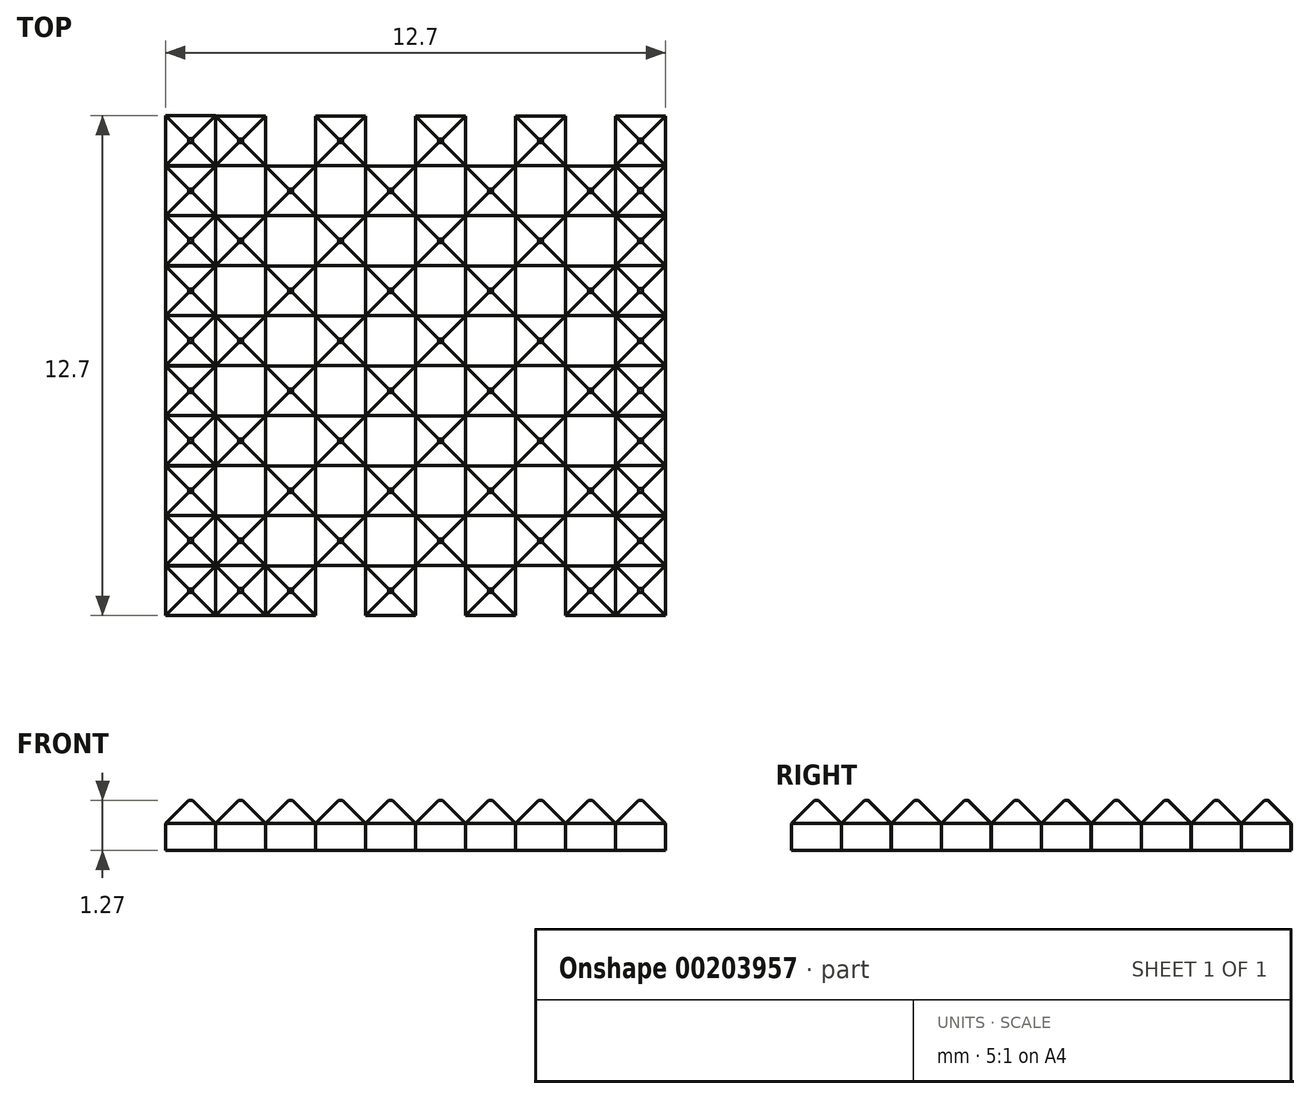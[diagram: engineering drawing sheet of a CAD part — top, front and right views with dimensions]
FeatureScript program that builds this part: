
annotation { "Feature Type Name" : "Feature", "Feature Type Description" : "" }
export const myFeature = defineFeature(function(context is Context, id is Id, definition is map)
    precondition{}
    {
        {
            var Q0;
            Q0=qCreatedBy(makeId("Top.planeOp"),FACE);
            var sketch = newSketch(context, id + "F0", { "sketchPlane" : qUnion([Q0])});
            skLineSegment(sketch, "E0.bottom", {"start": v(0, 0) * mm, "end": v(1.27, 0) * mm});
            skLineSegment(sketch, "E0.top", {"start": v(0, 1.27) * mm, "end": v(1.27, 1.27) * mm});
            skLineSegment(sketch, "E0.left", {"start": v(0, 0) * mm, "end": v(0, 1.27) * mm});
            skLineSegment(sketch, "E0.right", {"start": v(1.27, 0) * mm, "end": v(1.27, 1.27) * mm});
            skLineSegment(sketch, "E1.0.1.0", {"start": v(1.27, 1.27) * mm, "end": v(1.27, 2.54) * mm});
            skLineSegment(sketch, "E1.0.1.1", {"start": v(0, 1.27) * mm, "end": v(0, 2.54) * mm});
            skLineSegment(sketch, "E1.0.1.2", {"start": v(0, 2.54) * mm, "end": v(1.27, 2.54) * mm});
            skLineSegment(sketch, "E1.0.2.0", {"start": v(1.27, 2.54) * mm, "end": v(1.27, 3.81) * mm});
            skLineSegment(sketch, "E1.0.2.1", {"start": v(0, 2.54) * mm, "end": v(0, 3.81) * mm});
            skLineSegment(sketch, "E1.0.2.2", {"start": v(0, 3.81) * mm, "end": v(1.27, 3.81) * mm});
            skLineSegment(sketch, "E1.0.2.3", {"start": v(0, 2.54) * mm, "end": v(1.27, 2.54) * mm});
            skLineSegment(sketch, "E1.0.3.0", {"start": v(1.27, 3.8) * mm, "end": v(1.27, 5.08) * mm});
            skLineSegment(sketch, "E1.0.3.1", {"start": v(0, 3.8) * mm, "end": v(0, 5.08) * mm});
            skLineSegment(sketch, "E1.0.3.2", {"start": v(0, 5.08) * mm, "end": v(1.27, 5.08) * mm});
            skLineSegment(sketch, "E1.0.3.3", {"start": v(0, 3.8) * mm, "end": v(1.27, 3.8) * mm});
            skLineSegment(sketch, "E1.0.4.0", {"start": v(1.27, 5.08) * mm, "end": v(1.27, 6.35) * mm});
            skLineSegment(sketch, "E1.0.4.1", {"start": v(0, 5.08) * mm, "end": v(0, 6.35) * mm});
            skLineSegment(sketch, "E1.0.4.2", {"start": v(0, 6.35) * mm, "end": v(1.27, 6.35) * mm});
            skLineSegment(sketch, "E1.0.4.3", {"start": v(0, 5.08) * mm, "end": v(1.27, 5.08) * mm});
            skLineSegment(sketch, "E1.0.5.0", {"start": v(1.27, 6.35) * mm, "end": v(1.27, 7.62) * mm});
            skLineSegment(sketch, "E1.0.5.1", {"start": v(0, 6.35) * mm, "end": v(0, 7.62) * mm});
            skLineSegment(sketch, "E1.0.5.2", {"start": v(0, 7.62) * mm, "end": v(1.27, 7.62) * mm});
            skLineSegment(sketch, "E1.0.5.3", {"start": v(0, 6.35) * mm, "end": v(1.27, 6.35) * mm});
            skLineSegment(sketch, "E1.0.6.0", {"start": v(1.27, 7.62) * mm, "end": v(1.27, 8.9) * mm});
            skLineSegment(sketch, "E1.0.6.1", {"start": v(0, 7.62) * mm, "end": v(0, 8.9) * mm});
            skLineSegment(sketch, "E1.0.6.2", {"start": v(0, 8.9) * mm, "end": v(1.27, 8.9) * mm});
            skLineSegment(sketch, "E1.0.6.3", {"start": v(0, 7.62) * mm, "end": v(1.27, 7.62) * mm});
            skLineSegment(sketch, "E1.0.7.0", {"start": v(1.27, 8.89) * mm, "end": v(1.27, 10.16) * mm});
            skLineSegment(sketch, "E1.0.7.1", {"start": v(0, 8.89) * mm, "end": v(0, 10.16) * mm});
            skLineSegment(sketch, "E1.0.7.2", {"start": v(0, 10.16) * mm, "end": v(1.27, 10.16) * mm});
            skLineSegment(sketch, "E1.0.7.3", {"start": v(0, 8.89) * mm, "end": v(1.27, 8.89) * mm});
            skLineSegment(sketch, "E1.0.8.0", {"start": v(1.27, 10.16) * mm, "end": v(1.27, 11.43) * mm});
            skLineSegment(sketch, "E1.0.8.1", {"start": v(0, 10.16) * mm, "end": v(0, 11.43) * mm});
            skLineSegment(sketch, "E1.0.8.2", {"start": v(0, 11.43) * mm, "end": v(1.27, 11.43) * mm});
            skLineSegment(sketch, "E1.0.8.3", {"start": v(0, 10.16) * mm, "end": v(1.27, 10.16) * mm});
            skLineSegment(sketch, "E1.0.9.0", {"start": v(1.27, 11.43) * mm, "end": v(1.27, 12.7) * mm});
            skLineSegment(sketch, "E1.0.9.1", {"start": v(0, 11.43) * mm, "end": v(0, 12.7) * mm});
            skLineSegment(sketch, "E1.0.9.2", {"start": v(0, 12.7) * mm, "end": v(1.27, 12.7) * mm});
            skLineSegment(sketch, "E1.0.9.3", {"start": v(0, 11.43) * mm, "end": v(1.27, 11.43) * mm});
            skLineSegment(sketch, "E1.1.0.0", {"start": v(2.54, 0) * mm, "end": v(2.54, 1.27) * mm});
            skLineSegment(sketch, "E1.1.0.2", {"start": v(1.27, 1.27) * mm, "end": v(2.54, 1.27) * mm});
            skLineSegment(sketch, "E1.1.0.3", {"start": v(1.27, 0) * mm, "end": v(2.54, 0) * mm});
            skLineSegment(sketch, "E1.1.1.0", {"start": v(2.54, 1.27) * mm, "end": v(2.54, 2.54) * mm});
            skLineSegment(sketch, "E1.1.1.1", {"start": v(1.27, 1.27) * mm, "end": v(1.27, 2.54) * mm});
            skLineSegment(sketch, "E1.1.1.2", {"start": v(1.27, 2.54) * mm, "end": v(2.54, 2.54) * mm});
            skLineSegment(sketch, "E1.1.1.3", {"start": v(1.27, 1.27) * mm, "end": v(2.54, 1.27) * mm});
            skLineSegment(sketch, "E1.1.2.0", {"start": v(2.54, 2.54) * mm, "end": v(2.54, 3.81) * mm});
            skLineSegment(sketch, "E1.1.2.1", {"start": v(1.27, 2.54) * mm, "end": v(1.27, 3.81) * mm});
            skLineSegment(sketch, "E1.1.2.2", {"start": v(1.27, 3.81) * mm, "end": v(2.54, 3.81) * mm});
            skLineSegment(sketch, "E1.1.2.3", {"start": v(1.27, 2.54) * mm, "end": v(2.54, 2.54) * mm});
            skLineSegment(sketch, "E1.1.3.0", {"start": v(2.54, 3.81) * mm, "end": v(2.54, 5.08) * mm});
            skLineSegment(sketch, "E1.1.3.1", {"start": v(1.27, 3.81) * mm, "end": v(1.27, 5.08) * mm});
            skLineSegment(sketch, "E1.1.3.2", {"start": v(1.27, 5.08) * mm, "end": v(2.54, 5.08) * mm});
            skLineSegment(sketch, "E1.1.3.3", {"start": v(1.27, 3.8) * mm, "end": v(2.54, 3.8) * mm});
            skLineSegment(sketch, "E1.1.4.0", {"start": v(2.54, 5.08) * mm, "end": v(2.54, 6.35) * mm});
            skLineSegment(sketch, "E1.1.4.1", {"start": v(1.27, 5.08) * mm, "end": v(1.27, 6.35) * mm});
            skLineSegment(sketch, "E1.1.4.2", {"start": v(1.27, 6.35) * mm, "end": v(2.54, 6.35) * mm});
            skLineSegment(sketch, "E1.1.4.3", {"start": v(1.27, 5.08) * mm, "end": v(2.54, 5.08) * mm});
            skLineSegment(sketch, "E1.1.5.0", {"start": v(2.54, 6.35) * mm, "end": v(2.54, 7.62) * mm});
            skLineSegment(sketch, "E1.1.5.1", {"start": v(1.27, 6.35) * mm, "end": v(1.27, 7.62) * mm});
            skLineSegment(sketch, "E1.1.5.2", {"start": v(1.27, 7.62) * mm, "end": v(2.54, 7.62) * mm});
            skLineSegment(sketch, "E1.1.5.3", {"start": v(1.27, 6.35) * mm, "end": v(2.54, 6.35) * mm});
            skLineSegment(sketch, "E1.1.6.0", {"start": v(2.54, 7.62) * mm, "end": v(2.54, 8.9) * mm});
            skLineSegment(sketch, "E1.1.6.1", {"start": v(1.27, 7.62) * mm, "end": v(1.27, 8.9) * mm});
            skLineSegment(sketch, "E1.1.6.2", {"start": v(1.27, 8.9) * mm, "end": v(2.54, 8.9) * mm});
            skLineSegment(sketch, "E1.1.6.3", {"start": v(1.27, 7.62) * mm, "end": v(2.54, 7.62) * mm});
            skLineSegment(sketch, "E1.1.7.0", {"start": v(2.54, 8.9) * mm, "end": v(2.54, 10.16) * mm});
            skLineSegment(sketch, "E1.1.7.1", {"start": v(1.27, 8.9) * mm, "end": v(1.27, 10.16) * mm});
            skLineSegment(sketch, "E1.1.7.2", {"start": v(1.27, 10.16) * mm, "end": v(2.54, 10.16) * mm});
            skLineSegment(sketch, "E1.1.7.3", {"start": v(1.27, 8.89) * mm, "end": v(2.54, 8.89) * mm});
            skLineSegment(sketch, "E1.1.8.0", {"start": v(2.54, 10.16) * mm, "end": v(2.54, 11.43) * mm});
            skLineSegment(sketch, "E1.1.8.1", {"start": v(1.27, 10.16) * mm, "end": v(1.27, 11.43) * mm});
            skLineSegment(sketch, "E1.1.8.2", {"start": v(1.27, 11.43) * mm, "end": v(2.54, 11.43) * mm});
            skLineSegment(sketch, "E1.1.8.3", {"start": v(1.27, 10.16) * mm, "end": v(2.54, 10.16) * mm});
            skLineSegment(sketch, "E1.1.9.0", {"start": v(2.54, 11.43) * mm, "end": v(2.54, 12.7) * mm});
            skLineSegment(sketch, "E1.1.9.1", {"start": v(1.27, 11.43) * mm, "end": v(1.27, 12.7) * mm});
            skLineSegment(sketch, "E1.1.9.2", {"start": v(1.27, 12.7) * mm, "end": v(2.54, 12.7) * mm});
            skLineSegment(sketch, "E1.1.9.3", {"start": v(1.27, 11.43) * mm, "end": v(2.54, 11.43) * mm});
            skLineSegment(sketch, "E1.2.0.0", {"start": v(3.81, 0) * mm, "end": v(3.81, 1.27) * mm});
            skLineSegment(sketch, "E1.2.0.1", {"start": v(2.54, 0) * mm, "end": v(2.54, 1.27) * mm});
            skLineSegment(sketch, "E1.2.0.2", {"start": v(2.54, 1.27) * mm, "end": v(3.81, 1.27) * mm});
            skLineSegment(sketch, "E1.2.0.3", {"start": v(2.54, 0) * mm, "end": v(3.81, 0) * mm});
            skLineSegment(sketch, "E1.2.1.0", {"start": v(3.81, 1.27) * mm, "end": v(3.81, 2.54) * mm});
            skLineSegment(sketch, "E1.2.1.1", {"start": v(2.54, 1.27) * mm, "end": v(2.54, 2.54) * mm});
            skLineSegment(sketch, "E1.2.1.2", {"start": v(2.54, 2.54) * mm, "end": v(3.81, 2.54) * mm});
            skLineSegment(sketch, "E1.2.1.3", {"start": v(2.54, 1.27) * mm, "end": v(3.81, 1.27) * mm});
            skLineSegment(sketch, "E1.2.2.0", {"start": v(3.81, 2.54) * mm, "end": v(3.81, 3.81) * mm});
            skLineSegment(sketch, "E1.2.2.1", {"start": v(2.54, 2.54) * mm, "end": v(2.54, 3.81) * mm});
            skLineSegment(sketch, "E1.2.2.2", {"start": v(2.54, 3.81) * mm, "end": v(3.81, 3.81) * mm});
            skLineSegment(sketch, "E1.2.2.3", {"start": v(2.54, 2.54) * mm, "end": v(3.81, 2.54) * mm});
            skLineSegment(sketch, "E1.2.3.0", {"start": v(3.81, 3.81) * mm, "end": v(3.81, 5.08) * mm});
            skLineSegment(sketch, "E1.2.3.1", {"start": v(2.54, 3.81) * mm, "end": v(2.54, 5.08) * mm});
            skLineSegment(sketch, "E1.2.3.2", {"start": v(2.54, 5.08) * mm, "end": v(3.81, 5.08) * mm});
            skLineSegment(sketch, "E1.2.3.3", {"start": v(2.54, 3.8) * mm, "end": v(3.81, 3.8) * mm});
            skLineSegment(sketch, "E1.2.4.0", {"start": v(3.81, 5.08) * mm, "end": v(3.81, 6.35) * mm});
            skLineSegment(sketch, "E1.2.4.1", {"start": v(2.54, 5.08) * mm, "end": v(2.54, 6.35) * mm});
            skLineSegment(sketch, "E1.2.4.2", {"start": v(2.54, 6.35) * mm, "end": v(3.81, 6.35) * mm});
            skLineSegment(sketch, "E1.2.4.3", {"start": v(2.54, 5.08) * mm, "end": v(3.81, 5.08) * mm});
            skLineSegment(sketch, "E1.2.5.0", {"start": v(3.81, 6.35) * mm, "end": v(3.81, 7.62) * mm});
            skLineSegment(sketch, "E1.2.5.1", {"start": v(2.54, 6.35) * mm, "end": v(2.54, 7.62) * mm});
            skLineSegment(sketch, "E1.2.5.2", {"start": v(2.54, 7.62) * mm, "end": v(3.81, 7.62) * mm});
            skLineSegment(sketch, "E1.2.5.3", {"start": v(2.54, 6.35) * mm, "end": v(3.81, 6.35) * mm});
            skLineSegment(sketch, "E1.2.6.0", {"start": v(3.81, 7.62) * mm, "end": v(3.81, 8.9) * mm});
            skLineSegment(sketch, "E1.2.6.1", {"start": v(2.54, 7.62) * mm, "end": v(2.54, 8.9) * mm});
            skLineSegment(sketch, "E1.2.6.2", {"start": v(2.54, 8.9) * mm, "end": v(3.81, 8.9) * mm});
            skLineSegment(sketch, "E1.2.6.3", {"start": v(2.54, 7.62) * mm, "end": v(3.81, 7.62) * mm});
            skLineSegment(sketch, "E1.2.7.0", {"start": v(3.81, 8.9) * mm, "end": v(3.81, 10.16) * mm});
            skLineSegment(sketch, "E1.2.7.1", {"start": v(2.54, 8.9) * mm, "end": v(2.54, 10.16) * mm});
            skLineSegment(sketch, "E1.2.7.2", {"start": v(2.54, 10.16) * mm, "end": v(3.81, 10.16) * mm});
            skLineSegment(sketch, "E1.2.7.3", {"start": v(2.54, 8.89) * mm, "end": v(3.81, 8.89) * mm});
            skLineSegment(sketch, "E1.2.8.0", {"start": v(3.81, 10.16) * mm, "end": v(3.81, 11.43) * mm});
            skLineSegment(sketch, "E1.2.8.1", {"start": v(2.54, 10.16) * mm, "end": v(2.54, 11.43) * mm});
            skLineSegment(sketch, "E1.2.8.2", {"start": v(2.54, 11.43) * mm, "end": v(3.81, 11.43) * mm});
            skLineSegment(sketch, "E1.2.8.3", {"start": v(2.54, 10.16) * mm, "end": v(3.81, 10.16) * mm});
            skLineSegment(sketch, "E1.2.9.0", {"start": v(3.81, 11.43) * mm, "end": v(3.81, 12.7) * mm});
            skLineSegment(sketch, "E1.2.9.1", {"start": v(2.54, 11.43) * mm, "end": v(2.54, 12.7) * mm});
            skLineSegment(sketch, "E1.2.9.2", {"start": v(2.54, 12.7) * mm, "end": v(3.81, 12.7) * mm});
            skLineSegment(sketch, "E1.2.9.3", {"start": v(2.54, 11.43) * mm, "end": v(3.81, 11.43) * mm});
            skLineSegment(sketch, "E1.3.0.0", {"start": v(5.08, 0) * mm, "end": v(5.08, 1.27) * mm});
            skLineSegment(sketch, "E1.3.0.1", {"start": v(3.81, 0) * mm, "end": v(3.81, 1.27) * mm});
            skLineSegment(sketch, "E1.3.0.2", {"start": v(3.81, 1.27) * mm, "end": v(5.08, 1.27) * mm});
            skLineSegment(sketch, "E1.3.0.3", {"start": v(3.81, 0) * mm, "end": v(5.08, 0) * mm});
            skLineSegment(sketch, "E1.3.1.0", {"start": v(5.08, 1.27) * mm, "end": v(5.08, 2.54) * mm});
            skLineSegment(sketch, "E1.3.1.1", {"start": v(3.81, 1.27) * mm, "end": v(3.81, 2.54) * mm});
            skLineSegment(sketch, "E1.3.1.2", {"start": v(3.81, 2.54) * mm, "end": v(5.08, 2.54) * mm});
            skLineSegment(sketch, "E1.3.1.3", {"start": v(3.81, 1.27) * mm, "end": v(5.08, 1.27) * mm});
            skLineSegment(sketch, "E1.3.2.0", {"start": v(5.08, 2.54) * mm, "end": v(5.08, 3.81) * mm});
            skLineSegment(sketch, "E1.3.2.1", {"start": v(3.81, 2.54) * mm, "end": v(3.81, 3.81) * mm});
            skLineSegment(sketch, "E1.3.2.2", {"start": v(3.81, 3.81) * mm, "end": v(5.08, 3.81) * mm});
            skLineSegment(sketch, "E1.3.2.3", {"start": v(3.81, 2.54) * mm, "end": v(5.08, 2.54) * mm});
            skLineSegment(sketch, "E1.3.3.0", {"start": v(5.08, 3.81) * mm, "end": v(5.08, 5.08) * mm});
            skLineSegment(sketch, "E1.3.3.1", {"start": v(3.81, 3.81) * mm, "end": v(3.81, 5.08) * mm});
            skLineSegment(sketch, "E1.3.3.2", {"start": v(3.81, 5.08) * mm, "end": v(5.08, 5.08) * mm});
            skLineSegment(sketch, "E1.3.3.3", {"start": v(3.81, 3.8) * mm, "end": v(5.08, 3.8) * mm});
            skLineSegment(sketch, "E1.3.4.0", {"start": v(5.08, 5.08) * mm, "end": v(5.08, 6.35) * mm});
            skLineSegment(sketch, "E1.3.4.1", {"start": v(3.81, 5.08) * mm, "end": v(3.81, 6.35) * mm});
            skLineSegment(sketch, "E1.3.4.2", {"start": v(3.81, 6.35) * mm, "end": v(5.08, 6.35) * mm});
            skLineSegment(sketch, "E1.3.4.3", {"start": v(3.81, 5.08) * mm, "end": v(5.08, 5.08) * mm});
            skLineSegment(sketch, "E1.3.5.0", {"start": v(5.08, 6.35) * mm, "end": v(5.08, 7.62) * mm});
            skLineSegment(sketch, "E1.3.5.1", {"start": v(3.81, 6.35) * mm, "end": v(3.81, 7.62) * mm});
            skLineSegment(sketch, "E1.3.5.2", {"start": v(3.81, 7.62) * mm, "end": v(5.08, 7.62) * mm});
            skLineSegment(sketch, "E1.3.5.3", {"start": v(3.81, 6.35) * mm, "end": v(5.08, 6.35) * mm});
            skLineSegment(sketch, "E1.3.6.0", {"start": v(5.08, 7.62) * mm, "end": v(5.08, 8.9) * mm});
            skLineSegment(sketch, "E1.3.6.1", {"start": v(3.81, 7.62) * mm, "end": v(3.81, 8.9) * mm});
            skLineSegment(sketch, "E1.3.6.2", {"start": v(3.81, 8.9) * mm, "end": v(5.08, 8.9) * mm});
            skLineSegment(sketch, "E1.3.6.3", {"start": v(3.81, 7.62) * mm, "end": v(5.08, 7.62) * mm});
            skLineSegment(sketch, "E1.3.7.0", {"start": v(5.08, 8.9) * mm, "end": v(5.08, 10.16) * mm});
            skLineSegment(sketch, "E1.3.7.1", {"start": v(3.81, 8.9) * mm, "end": v(3.81, 10.16) * mm});
            skLineSegment(sketch, "E1.3.7.2", {"start": v(3.81, 10.16) * mm, "end": v(5.08, 10.16) * mm});
            skLineSegment(sketch, "E1.3.7.3", {"start": v(3.81, 8.89) * mm, "end": v(5.08, 8.89) * mm});
            skLineSegment(sketch, "E1.3.8.0", {"start": v(5.08, 10.16) * mm, "end": v(5.08, 11.43) * mm});
            skLineSegment(sketch, "E1.3.8.1", {"start": v(3.81, 10.16) * mm, "end": v(3.81, 11.43) * mm});
            skLineSegment(sketch, "E1.3.8.2", {"start": v(3.81, 11.43) * mm, "end": v(5.08, 11.43) * mm});
            skLineSegment(sketch, "E1.3.8.3", {"start": v(3.81, 10.16) * mm, "end": v(5.08, 10.16) * mm});
            skLineSegment(sketch, "E1.3.9.0", {"start": v(5.08, 11.43) * mm, "end": v(5.08, 12.7) * mm});
            skLineSegment(sketch, "E1.3.9.1", {"start": v(3.81, 11.43) * mm, "end": v(3.81, 12.7) * mm});
            skLineSegment(sketch, "E1.3.9.2", {"start": v(3.81, 12.7) * mm, "end": v(5.08, 12.7) * mm});
            skLineSegment(sketch, "E1.3.9.3", {"start": v(3.81, 11.43) * mm, "end": v(5.08, 11.43) * mm});
            skLineSegment(sketch, "E1.4.0.0", {"start": v(6.35, 0) * mm, "end": v(6.35, 1.27) * mm});
            skLineSegment(sketch, "E1.4.0.1", {"start": v(5.08, 0) * mm, "end": v(5.08, 1.27) * mm});
            skLineSegment(sketch, "E1.4.0.2", {"start": v(5.08, 1.27) * mm, "end": v(6.35, 1.27) * mm});
            skLineSegment(sketch, "E1.4.0.3", {"start": v(5.08, 0) * mm, "end": v(6.35, 0) * mm});
            skLineSegment(sketch, "E1.4.1.0", {"start": v(6.35, 1.27) * mm, "end": v(6.35, 2.54) * mm});
            skLineSegment(sketch, "E1.4.1.1", {"start": v(5.08, 1.27) * mm, "end": v(5.08, 2.54) * mm});
            skLineSegment(sketch, "E1.4.1.2", {"start": v(5.08, 2.54) * mm, "end": v(6.35, 2.54) * mm});
            skLineSegment(sketch, "E1.4.1.3", {"start": v(5.08, 1.27) * mm, "end": v(6.35, 1.27) * mm});
            skLineSegment(sketch, "E1.4.2.0", {"start": v(6.35, 2.54) * mm, "end": v(6.35, 3.81) * mm});
            skLineSegment(sketch, "E1.4.2.1", {"start": v(5.08, 2.54) * mm, "end": v(5.08, 3.81) * mm});
            skLineSegment(sketch, "E1.4.2.2", {"start": v(5.08, 3.81) * mm, "end": v(6.35, 3.81) * mm});
            skLineSegment(sketch, "E1.4.2.3", {"start": v(5.08, 2.54) * mm, "end": v(6.35, 2.54) * mm});
            skLineSegment(sketch, "E1.4.3.0", {"start": v(6.35, 3.81) * mm, "end": v(6.35, 5.08) * mm});
            skLineSegment(sketch, "E1.4.3.1", {"start": v(5.08, 3.81) * mm, "end": v(5.08, 5.08) * mm});
            skLineSegment(sketch, "E1.4.3.2", {"start": v(5.08, 5.08) * mm, "end": v(6.35, 5.08) * mm});
            skLineSegment(sketch, "E1.4.3.3", {"start": v(5.08, 3.8) * mm, "end": v(6.35, 3.8) * mm});
            skLineSegment(sketch, "E1.4.4.0", {"start": v(6.35, 5.08) * mm, "end": v(6.35, 6.35) * mm});
            skLineSegment(sketch, "E1.4.4.1", {"start": v(5.08, 5.08) * mm, "end": v(5.08, 6.35) * mm});
            skLineSegment(sketch, "E1.4.4.2", {"start": v(5.08, 6.35) * mm, "end": v(6.35, 6.35) * mm});
            skLineSegment(sketch, "E1.4.4.3", {"start": v(5.08, 5.08) * mm, "end": v(6.35, 5.08) * mm});
            skLineSegment(sketch, "E1.4.5.0", {"start": v(6.35, 6.35) * mm, "end": v(6.35, 7.62) * mm});
            skLineSegment(sketch, "E1.4.5.1", {"start": v(5.08, 6.35) * mm, "end": v(5.08, 7.62) * mm});
            skLineSegment(sketch, "E1.4.5.2", {"start": v(5.08, 7.62) * mm, "end": v(6.35, 7.62) * mm});
            skLineSegment(sketch, "E1.4.5.3", {"start": v(5.08, 6.35) * mm, "end": v(6.35, 6.35) * mm});
            skLineSegment(sketch, "E1.4.6.0", {"start": v(6.35, 7.62) * mm, "end": v(6.35, 8.9) * mm});
            skLineSegment(sketch, "E1.4.6.1", {"start": v(5.08, 7.62) * mm, "end": v(5.08, 8.9) * mm});
            skLineSegment(sketch, "E1.4.6.2", {"start": v(5.08, 8.9) * mm, "end": v(6.35, 8.9) * mm});
            skLineSegment(sketch, "E1.4.6.3", {"start": v(5.08, 7.62) * mm, "end": v(6.35, 7.62) * mm});
            skLineSegment(sketch, "E1.4.7.0", {"start": v(6.35, 8.9) * mm, "end": v(6.35, 10.16) * mm});
            skLineSegment(sketch, "E1.4.7.1", {"start": v(5.08, 8.9) * mm, "end": v(5.08, 10.16) * mm});
            skLineSegment(sketch, "E1.4.7.2", {"start": v(5.08, 10.16) * mm, "end": v(6.35, 10.16) * mm});
            skLineSegment(sketch, "E1.4.7.3", {"start": v(5.08, 8.89) * mm, "end": v(6.35, 8.89) * mm});
            skLineSegment(sketch, "E1.4.8.0", {"start": v(6.35, 10.16) * mm, "end": v(6.35, 11.43) * mm});
            skLineSegment(sketch, "E1.4.8.1", {"start": v(5.08, 10.16) * mm, "end": v(5.08, 11.43) * mm});
            skLineSegment(sketch, "E1.4.8.2", {"start": v(5.08, 11.43) * mm, "end": v(6.35, 11.43) * mm});
            skLineSegment(sketch, "E1.4.8.3", {"start": v(5.08, 10.16) * mm, "end": v(6.35, 10.16) * mm});
            skLineSegment(sketch, "E1.4.9.0", {"start": v(6.35, 11.43) * mm, "end": v(6.35, 12.7) * mm});
            skLineSegment(sketch, "E1.4.9.1", {"start": v(5.08, 11.43) * mm, "end": v(5.08, 12.7) * mm});
            skLineSegment(sketch, "E1.4.9.2", {"start": v(5.08, 12.7) * mm, "end": v(6.35, 12.7) * mm});
            skLineSegment(sketch, "E1.4.9.3", {"start": v(5.08, 11.43) * mm, "end": v(6.35, 11.43) * mm});
            skLineSegment(sketch, "E1.5.0.0", {"start": v(7.62, 0) * mm, "end": v(7.62, 1.27) * mm});
            skLineSegment(sketch, "E1.5.0.1", {"start": v(6.35, 0) * mm, "end": v(6.35, 1.27) * mm});
            skLineSegment(sketch, "E1.5.0.2", {"start": v(6.35, 1.27) * mm, "end": v(7.62, 1.27) * mm});
            skLineSegment(sketch, "E1.5.0.3", {"start": v(6.35, 0) * mm, "end": v(7.62, 0) * mm});
            skLineSegment(sketch, "E1.5.1.0", {"start": v(7.62, 1.27) * mm, "end": v(7.62, 2.54) * mm});
            skLineSegment(sketch, "E1.5.1.1", {"start": v(6.35, 1.27) * mm, "end": v(6.35, 2.54) * mm});
            skLineSegment(sketch, "E1.5.1.2", {"start": v(6.35, 2.54) * mm, "end": v(7.62, 2.54) * mm});
            skLineSegment(sketch, "E1.5.1.3", {"start": v(6.35, 1.27) * mm, "end": v(7.62, 1.27) * mm});
            skLineSegment(sketch, "E1.5.2.0", {"start": v(7.62, 2.54) * mm, "end": v(7.62, 3.81) * mm});
            skLineSegment(sketch, "E1.5.2.1", {"start": v(6.35, 2.54) * mm, "end": v(6.35, 3.81) * mm});
            skLineSegment(sketch, "E1.5.2.2", {"start": v(6.35, 3.81) * mm, "end": v(7.62, 3.81) * mm});
            skLineSegment(sketch, "E1.5.2.3", {"start": v(6.35, 2.54) * mm, "end": v(7.62, 2.54) * mm});
            skLineSegment(sketch, "E1.5.3.0", {"start": v(7.62, 3.81) * mm, "end": v(7.62, 5.08) * mm});
            skLineSegment(sketch, "E1.5.3.1", {"start": v(6.35, 3.81) * mm, "end": v(6.35, 5.08) * mm});
            skLineSegment(sketch, "E1.5.3.2", {"start": v(6.35, 5.08) * mm, "end": v(7.62, 5.08) * mm});
            skLineSegment(sketch, "E1.5.3.3", {"start": v(6.35, 3.8) * mm, "end": v(7.62, 3.8) * mm});
            skLineSegment(sketch, "E1.5.4.0", {"start": v(7.62, 5.08) * mm, "end": v(7.62, 6.35) * mm});
            skLineSegment(sketch, "E1.5.4.1", {"start": v(6.35, 5.08) * mm, "end": v(6.35, 6.35) * mm});
            skLineSegment(sketch, "E1.5.4.2", {"start": v(6.35, 6.35) * mm, "end": v(7.62, 6.35) * mm});
            skLineSegment(sketch, "E1.5.4.3", {"start": v(6.35, 5.08) * mm, "end": v(7.62, 5.08) * mm});
            skLineSegment(sketch, "E1.5.5.0", {"start": v(7.62, 6.35) * mm, "end": v(7.62, 7.62) * mm});
            skLineSegment(sketch, "E1.5.5.1", {"start": v(6.35, 6.35) * mm, "end": v(6.35, 7.62) * mm});
            skLineSegment(sketch, "E1.5.5.2", {"start": v(6.35, 7.62) * mm, "end": v(7.62, 7.62) * mm});
            skLineSegment(sketch, "E1.5.5.3", {"start": v(6.35, 6.35) * mm, "end": v(7.62, 6.35) * mm});
            skLineSegment(sketch, "E1.5.6.0", {"start": v(7.62, 7.62) * mm, "end": v(7.62, 8.9) * mm});
            skLineSegment(sketch, "E1.5.6.1", {"start": v(6.35, 7.62) * mm, "end": v(6.35, 8.9) * mm});
            skLineSegment(sketch, "E1.5.6.2", {"start": v(6.35, 8.9) * mm, "end": v(7.62, 8.9) * mm});
            skLineSegment(sketch, "E1.5.6.3", {"start": v(6.35, 7.62) * mm, "end": v(7.62, 7.62) * mm});
            skLineSegment(sketch, "E1.5.7.0", {"start": v(7.62, 8.9) * mm, "end": v(7.62, 10.16) * mm});
            skLineSegment(sketch, "E1.5.7.1", {"start": v(6.35, 8.9) * mm, "end": v(6.35, 10.16) * mm});
            skLineSegment(sketch, "E1.5.7.2", {"start": v(6.35, 10.16) * mm, "end": v(7.62, 10.16) * mm});
            skLineSegment(sketch, "E1.5.7.3", {"start": v(6.35, 8.89) * mm, "end": v(7.62, 8.89) * mm});
            skLineSegment(sketch, "E1.5.8.0", {"start": v(7.62, 10.16) * mm, "end": v(7.62, 11.43) * mm});
            skLineSegment(sketch, "E1.5.8.1", {"start": v(6.35, 10.16) * mm, "end": v(6.35, 11.43) * mm});
            skLineSegment(sketch, "E1.5.8.2", {"start": v(6.35, 11.43) * mm, "end": v(7.62, 11.43) * mm});
            skLineSegment(sketch, "E1.5.8.3", {"start": v(6.35, 10.16) * mm, "end": v(7.62, 10.16) * mm});
            skLineSegment(sketch, "E1.5.9.0", {"start": v(7.62, 11.43) * mm, "end": v(7.62, 12.7) * mm});
            skLineSegment(sketch, "E1.5.9.1", {"start": v(6.35, 11.43) * mm, "end": v(6.35, 12.7) * mm});
            skLineSegment(sketch, "E1.5.9.2", {"start": v(6.35, 12.7) * mm, "end": v(7.62, 12.7) * mm});
            skLineSegment(sketch, "E1.5.9.3", {"start": v(6.35, 11.43) * mm, "end": v(7.62, 11.43) * mm});
            skLineSegment(sketch, "E1.6.0.0", {"start": v(8.9, 0) * mm, "end": v(8.9, 1.27) * mm});
            skLineSegment(sketch, "E1.6.0.1", {"start": v(7.62, 0) * mm, "end": v(7.62, 1.27) * mm});
            skLineSegment(sketch, "E1.6.0.2", {"start": v(7.62, 1.27) * mm, "end": v(8.9, 1.27) * mm});
            skLineSegment(sketch, "E1.6.0.3", {"start": v(7.62, 0) * mm, "end": v(8.9, 0) * mm});
            skLineSegment(sketch, "E1.6.1.0", {"start": v(8.9, 1.27) * mm, "end": v(8.9, 2.54) * mm});
            skLineSegment(sketch, "E1.6.1.1", {"start": v(7.62, 1.27) * mm, "end": v(7.62, 2.54) * mm});
            skLineSegment(sketch, "E1.6.1.2", {"start": v(7.62, 2.54) * mm, "end": v(8.9, 2.54) * mm});
            skLineSegment(sketch, "E1.6.1.3", {"start": v(7.62, 1.27) * mm, "end": v(8.9, 1.27) * mm});
            skLineSegment(sketch, "E1.6.2.0", {"start": v(8.9, 2.54) * mm, "end": v(8.9, 3.81) * mm});
            skLineSegment(sketch, "E1.6.2.1", {"start": v(7.62, 2.54) * mm, "end": v(7.62, 3.81) * mm});
            skLineSegment(sketch, "E1.6.2.2", {"start": v(7.62, 3.81) * mm, "end": v(8.9, 3.81) * mm});
            skLineSegment(sketch, "E1.6.2.3", {"start": v(7.62, 2.54) * mm, "end": v(8.9, 2.54) * mm});
            skLineSegment(sketch, "E1.6.3.0", {"start": v(8.9, 3.81) * mm, "end": v(8.9, 5.08) * mm});
            skLineSegment(sketch, "E1.6.3.1", {"start": v(7.62, 3.81) * mm, "end": v(7.62, 5.08) * mm});
            skLineSegment(sketch, "E1.6.3.2", {"start": v(7.62, 5.08) * mm, "end": v(8.9, 5.08) * mm});
            skLineSegment(sketch, "E1.6.3.3", {"start": v(7.62, 3.8) * mm, "end": v(8.9, 3.8) * mm});
            skLineSegment(sketch, "E1.6.4.0", {"start": v(8.9, 5.08) * mm, "end": v(8.9, 6.35) * mm});
            skLineSegment(sketch, "E1.6.4.1", {"start": v(7.62, 5.08) * mm, "end": v(7.62, 6.35) * mm});
            skLineSegment(sketch, "E1.6.4.2", {"start": v(7.62, 6.35) * mm, "end": v(8.9, 6.35) * mm});
            skLineSegment(sketch, "E1.6.4.3", {"start": v(7.62, 5.08) * mm, "end": v(8.9, 5.08) * mm});
            skLineSegment(sketch, "E1.6.5.0", {"start": v(8.9, 6.35) * mm, "end": v(8.9, 7.62) * mm});
            skLineSegment(sketch, "E1.6.5.1", {"start": v(7.62, 6.35) * mm, "end": v(7.62, 7.62) * mm});
            skLineSegment(sketch, "E1.6.5.2", {"start": v(7.62, 7.62) * mm, "end": v(8.9, 7.62) * mm});
            skLineSegment(sketch, "E1.6.5.3", {"start": v(7.62, 6.35) * mm, "end": v(8.9, 6.35) * mm});
            skLineSegment(sketch, "E1.6.6.0", {"start": v(8.9, 7.62) * mm, "end": v(8.9, 8.9) * mm});
            skLineSegment(sketch, "E1.6.6.1", {"start": v(7.62, 7.62) * mm, "end": v(7.62, 8.9) * mm});
            skLineSegment(sketch, "E1.6.6.2", {"start": v(7.62, 8.9) * mm, "end": v(8.9, 8.9) * mm});
            skLineSegment(sketch, "E1.6.6.3", {"start": v(7.62, 7.62) * mm, "end": v(8.9, 7.62) * mm});
            skLineSegment(sketch, "E1.6.7.0", {"start": v(8.9, 8.9) * mm, "end": v(8.9, 10.16) * mm});
            skLineSegment(sketch, "E1.6.7.1", {"start": v(7.62, 8.9) * mm, "end": v(7.62, 10.16) * mm});
            skLineSegment(sketch, "E1.6.7.2", {"start": v(7.62, 10.16) * mm, "end": v(8.9, 10.16) * mm});
            skLineSegment(sketch, "E1.6.7.3", {"start": v(7.62, 8.89) * mm, "end": v(8.9, 8.89) * mm});
            skLineSegment(sketch, "E1.6.8.0", {"start": v(8.9, 10.16) * mm, "end": v(8.9, 11.43) * mm});
            skLineSegment(sketch, "E1.6.8.1", {"start": v(7.62, 10.16) * mm, "end": v(7.62, 11.43) * mm});
            skLineSegment(sketch, "E1.6.8.2", {"start": v(7.62, 11.43) * mm, "end": v(8.9, 11.43) * mm});
            skLineSegment(sketch, "E1.6.8.3", {"start": v(7.62, 10.16) * mm, "end": v(8.9, 10.16) * mm});
            skLineSegment(sketch, "E1.6.9.0", {"start": v(8.9, 11.43) * mm, "end": v(8.9, 12.7) * mm});
            skLineSegment(sketch, "E1.6.9.1", {"start": v(7.62, 11.43) * mm, "end": v(7.62, 12.7) * mm});
            skLineSegment(sketch, "E1.6.9.2", {"start": v(7.62, 12.7) * mm, "end": v(8.9, 12.7) * mm});
            skLineSegment(sketch, "E1.6.9.3", {"start": v(7.62, 11.43) * mm, "end": v(8.9, 11.43) * mm});
            skLineSegment(sketch, "E1.7.0.0", {"start": v(10.16, 0) * mm, "end": v(10.16, 1.27) * mm});
            skLineSegment(sketch, "E1.7.0.1", {"start": v(8.9, 0) * mm, "end": v(8.9, 1.27) * mm});
            skLineSegment(sketch, "E1.7.0.2", {"start": v(8.9, 1.27) * mm, "end": v(10.16, 1.27) * mm});
            skLineSegment(sketch, "E1.7.0.3", {"start": v(8.9, 0) * mm, "end": v(10.16, 0) * mm});
            skLineSegment(sketch, "E1.7.1.0", {"start": v(10.16, 1.27) * mm, "end": v(10.16, 2.54) * mm});
            skLineSegment(sketch, "E1.7.1.1", {"start": v(8.9, 1.27) * mm, "end": v(8.9, 2.54) * mm});
            skLineSegment(sketch, "E1.7.1.2", {"start": v(8.9, 2.54) * mm, "end": v(10.16, 2.54) * mm});
            skLineSegment(sketch, "E1.7.1.3", {"start": v(8.9, 1.27) * mm, "end": v(10.16, 1.27) * mm});
            skLineSegment(sketch, "E1.7.2.0", {"start": v(10.16, 2.54) * mm, "end": v(10.16, 3.81) * mm});
            skLineSegment(sketch, "E1.7.2.1", {"start": v(8.9, 2.54) * mm, "end": v(8.9, 3.81) * mm});
            skLineSegment(sketch, "E1.7.2.2", {"start": v(8.9, 3.81) * mm, "end": v(10.16, 3.81) * mm});
            skLineSegment(sketch, "E1.7.2.3", {"start": v(8.9, 2.54) * mm, "end": v(10.16, 2.54) * mm});
            skLineSegment(sketch, "E1.7.3.0", {"start": v(10.16, 3.81) * mm, "end": v(10.16, 5.08) * mm});
            skLineSegment(sketch, "E1.7.3.1", {"start": v(8.9, 3.81) * mm, "end": v(8.9, 5.08) * mm});
            skLineSegment(sketch, "E1.7.3.2", {"start": v(8.9, 5.08) * mm, "end": v(10.16, 5.08) * mm});
            skLineSegment(sketch, "E1.7.3.3", {"start": v(8.9, 3.8) * mm, "end": v(10.16, 3.8) * mm});
            skLineSegment(sketch, "E1.7.4.0", {"start": v(10.16, 5.08) * mm, "end": v(10.16, 6.35) * mm});
            skLineSegment(sketch, "E1.7.4.1", {"start": v(8.89, 5.08) * mm, "end": v(8.89, 6.35) * mm});
            skLineSegment(sketch, "E1.7.4.2", {"start": v(8.9, 6.35) * mm, "end": v(10.16, 6.35) * mm});
            skLineSegment(sketch, "E1.7.4.3", {"start": v(8.9, 5.08) * mm, "end": v(10.16, 5.08) * mm});
            skLineSegment(sketch, "E1.7.5.0", {"start": v(10.16, 6.35) * mm, "end": v(10.16, 7.62) * mm});
            skLineSegment(sketch, "E1.7.5.1", {"start": v(8.89, 6.35) * mm, "end": v(8.89, 7.62) * mm});
            skLineSegment(sketch, "E1.7.5.2", {"start": v(8.9, 7.62) * mm, "end": v(10.16, 7.62) * mm});
            skLineSegment(sketch, "E1.7.5.3", {"start": v(8.9, 6.35) * mm, "end": v(10.16, 6.35) * mm});
            skLineSegment(sketch, "E1.7.6.0", {"start": v(10.16, 7.62) * mm, "end": v(10.16, 8.9) * mm});
            skLineSegment(sketch, "E1.7.6.1", {"start": v(8.9, 7.62) * mm, "end": v(8.9, 8.9) * mm});
            skLineSegment(sketch, "E1.7.6.2", {"start": v(8.9, 8.9) * mm, "end": v(10.16, 8.9) * mm});
            skLineSegment(sketch, "E1.7.6.3", {"start": v(8.9, 7.62) * mm, "end": v(10.16, 7.62) * mm});
            skLineSegment(sketch, "E1.7.7.0", {"start": v(10.16, 8.9) * mm, "end": v(10.16, 10.16) * mm});
            skLineSegment(sketch, "E1.7.7.1", {"start": v(8.9, 8.9) * mm, "end": v(8.9, 10.16) * mm});
            skLineSegment(sketch, "E1.7.7.2", {"start": v(8.9, 10.16) * mm, "end": v(10.16, 10.16) * mm});
            skLineSegment(sketch, "E1.7.7.3", {"start": v(8.9, 8.89) * mm, "end": v(10.16, 8.89) * mm});
            skLineSegment(sketch, "E1.7.8.0", {"start": v(10.16, 10.16) * mm, "end": v(10.16, 11.43) * mm});
            skLineSegment(sketch, "E1.7.8.1", {"start": v(8.9, 10.16) * mm, "end": v(8.9, 11.43) * mm});
            skLineSegment(sketch, "E1.7.8.2", {"start": v(8.9, 11.43) * mm, "end": v(10.16, 11.43) * mm});
            skLineSegment(sketch, "E1.7.8.3", {"start": v(8.9, 10.16) * mm, "end": v(10.16, 10.16) * mm});
            skLineSegment(sketch, "E1.7.9.0", {"start": v(10.16, 11.43) * mm, "end": v(10.16, 12.7) * mm});
            skLineSegment(sketch, "E1.7.9.1", {"start": v(8.9, 11.43) * mm, "end": v(8.9, 12.7) * mm});
            skLineSegment(sketch, "E1.7.9.2", {"start": v(8.9, 12.7) * mm, "end": v(10.16, 12.7) * mm});
            skLineSegment(sketch, "E1.7.9.3", {"start": v(8.9, 11.43) * mm, "end": v(10.16, 11.43) * mm});
            skLineSegment(sketch, "E1.8.0.0", {"start": v(11.43, 0) * mm, "end": v(11.43, 1.27) * mm});
            skLineSegment(sketch, "E1.8.0.1", {"start": v(10.16, 0) * mm, "end": v(10.16, 1.27) * mm});
            skLineSegment(sketch, "E1.8.0.2", {"start": v(10.16, 1.27) * mm, "end": v(11.43, 1.27) * mm});
            skLineSegment(sketch, "E1.8.0.3", {"start": v(10.16, 0) * mm, "end": v(11.43, 0) * mm});
            skLineSegment(sketch, "E1.8.1.0", {"start": v(11.43, 1.27) * mm, "end": v(11.43, 2.54) * mm});
            skLineSegment(sketch, "E1.8.1.1", {"start": v(10.16, 1.27) * mm, "end": v(10.16, 2.54) * mm});
            skLineSegment(sketch, "E1.8.1.2", {"start": v(10.16, 2.54) * mm, "end": v(11.43, 2.54) * mm});
            skLineSegment(sketch, "E1.8.1.3", {"start": v(10.16, 1.27) * mm, "end": v(11.43, 1.27) * mm});
            skLineSegment(sketch, "E1.8.2.0", {"start": v(11.43, 2.54) * mm, "end": v(11.43, 3.81) * mm});
            skLineSegment(sketch, "E1.8.2.1", {"start": v(10.16, 2.54) * mm, "end": v(10.16, 3.81) * mm});
            skLineSegment(sketch, "E1.8.2.2", {"start": v(10.16, 3.81) * mm, "end": v(11.43, 3.81) * mm});
            skLineSegment(sketch, "E1.8.2.3", {"start": v(10.16, 2.54) * mm, "end": v(11.43, 2.54) * mm});
            skLineSegment(sketch, "E1.8.3.0", {"start": v(11.43, 3.81) * mm, "end": v(11.43, 5.08) * mm});
            skLineSegment(sketch, "E1.8.3.1", {"start": v(10.16, 3.81) * mm, "end": v(10.16, 5.08) * mm});
            skLineSegment(sketch, "E1.8.3.2", {"start": v(10.16, 5.08) * mm, "end": v(11.43, 5.08) * mm});
            skLineSegment(sketch, "E1.8.3.3", {"start": v(10.16, 3.8) * mm, "end": v(11.43, 3.8) * mm});
            skLineSegment(sketch, "E1.8.4.0", {"start": v(11.43, 5.08) * mm, "end": v(11.43, 6.35) * mm});
            skLineSegment(sketch, "E1.8.4.1", {"start": v(10.16, 5.08) * mm, "end": v(10.16, 6.35) * mm});
            skLineSegment(sketch, "E1.8.4.2", {"start": v(10.16, 6.35) * mm, "end": v(11.43, 6.35) * mm});
            skLineSegment(sketch, "E1.8.4.3", {"start": v(10.16, 5.08) * mm, "end": v(11.43, 5.08) * mm});
            skLineSegment(sketch, "E1.8.5.0", {"start": v(11.43, 6.35) * mm, "end": v(11.43, 7.62) * mm});
            skLineSegment(sketch, "E1.8.5.1", {"start": v(10.16, 6.35) * mm, "end": v(10.16, 7.62) * mm});
            skLineSegment(sketch, "E1.8.5.2", {"start": v(10.16, 7.62) * mm, "end": v(11.43, 7.62) * mm});
            skLineSegment(sketch, "E1.8.5.3", {"start": v(10.16, 6.35) * mm, "end": v(11.43, 6.35) * mm});
            skLineSegment(sketch, "E1.8.6.0", {"start": v(11.43, 7.62) * mm, "end": v(11.43, 8.9) * mm});
            skLineSegment(sketch, "E1.8.6.1", {"start": v(10.16, 7.62) * mm, "end": v(10.16, 8.9) * mm});
            skLineSegment(sketch, "E1.8.6.2", {"start": v(10.16, 8.9) * mm, "end": v(11.43, 8.9) * mm});
            skLineSegment(sketch, "E1.8.6.3", {"start": v(10.16, 7.62) * mm, "end": v(11.43, 7.62) * mm});
            skLineSegment(sketch, "E1.8.7.0", {"start": v(11.43, 8.9) * mm, "end": v(11.43, 10.16) * mm});
            skLineSegment(sketch, "E1.8.7.1", {"start": v(10.16, 8.9) * mm, "end": v(10.16, 10.16) * mm});
            skLineSegment(sketch, "E1.8.7.2", {"start": v(10.16, 10.16) * mm, "end": v(11.43, 10.16) * mm});
            skLineSegment(sketch, "E1.8.7.3", {"start": v(10.16, 8.89) * mm, "end": v(11.43, 8.89) * mm});
            skLineSegment(sketch, "E1.8.8.0", {"start": v(11.43, 10.16) * mm, "end": v(11.43, 11.43) * mm});
            skLineSegment(sketch, "E1.8.8.1", {"start": v(10.16, 10.16) * mm, "end": v(10.16, 11.43) * mm});
            skLineSegment(sketch, "E1.8.8.2", {"start": v(10.16, 11.43) * mm, "end": v(11.43, 11.43) * mm});
            skLineSegment(sketch, "E1.8.8.3", {"start": v(10.16, 10.16) * mm, "end": v(11.43, 10.16) * mm});
            skLineSegment(sketch, "E1.8.9.0", {"start": v(11.43, 11.43) * mm, "end": v(11.43, 12.7) * mm});
            skLineSegment(sketch, "E1.8.9.1", {"start": v(10.16, 11.43) * mm, "end": v(10.16, 12.7) * mm});
            skLineSegment(sketch, "E1.8.9.2", {"start": v(10.16, 12.7) * mm, "end": v(11.43, 12.7) * mm});
            skLineSegment(sketch, "E1.8.9.3", {"start": v(10.16, 11.43) * mm, "end": v(11.43, 11.43) * mm});
            skLineSegment(sketch, "E1.9.0.0", {"start": v(12.7, 0) * mm, "end": v(12.7, 1.27) * mm});
            skLineSegment(sketch, "E1.9.0.1", {"start": v(11.43, 0) * mm, "end": v(11.43, 1.27) * mm});
            skLineSegment(sketch, "E1.9.0.2", {"start": v(11.43, 1.27) * mm, "end": v(12.7, 1.27) * mm});
            skLineSegment(sketch, "E1.9.0.3", {"start": v(11.43, 0) * mm, "end": v(12.7, 0) * mm});
            skLineSegment(sketch, "E1.9.1.0", {"start": v(12.7, 1.27) * mm, "end": v(12.7, 2.54) * mm});
            skLineSegment(sketch, "E1.9.1.1", {"start": v(11.43, 1.27) * mm, "end": v(11.43, 2.54) * mm});
            skLineSegment(sketch, "E1.9.1.2", {"start": v(11.43, 2.54) * mm, "end": v(12.7, 2.54) * mm});
            skLineSegment(sketch, "E1.9.1.3", {"start": v(11.43, 1.27) * mm, "end": v(12.7, 1.27) * mm});
            skLineSegment(sketch, "E1.9.2.0", {"start": v(12.7, 2.54) * mm, "end": v(12.7, 3.81) * mm});
            skLineSegment(sketch, "E1.9.2.1", {"start": v(11.43, 2.54) * mm, "end": v(11.43, 3.81) * mm});
            skLineSegment(sketch, "E1.9.2.2", {"start": v(11.43, 3.81) * mm, "end": v(12.7, 3.81) * mm});
            skLineSegment(sketch, "E1.9.2.3", {"start": v(11.43, 2.54) * mm, "end": v(12.7, 2.54) * mm});
            skLineSegment(sketch, "E1.9.3.0", {"start": v(12.7, 3.81) * mm, "end": v(12.7, 5.08) * mm});
            skLineSegment(sketch, "E1.9.3.1", {"start": v(11.43, 3.81) * mm, "end": v(11.43, 5.08) * mm});
            skLineSegment(sketch, "E1.9.3.2", {"start": v(11.43, 5.08) * mm, "end": v(12.7, 5.08) * mm});
            skLineSegment(sketch, "E1.9.3.3", {"start": v(11.43, 3.8) * mm, "end": v(12.7, 3.8) * mm});
            skLineSegment(sketch, "E1.9.4.0", {"start": v(12.7, 5.08) * mm, "end": v(12.7, 6.35) * mm});
            skLineSegment(sketch, "E1.9.4.1", {"start": v(11.43, 5.08) * mm, "end": v(11.43, 6.35) * mm});
            skLineSegment(sketch, "E1.9.4.2", {"start": v(11.43, 6.35) * mm, "end": v(12.7, 6.35) * mm});
            skLineSegment(sketch, "E1.9.4.3", {"start": v(11.43, 5.08) * mm, "end": v(12.7, 5.08) * mm});
            skLineSegment(sketch, "E1.9.5.0", {"start": v(12.7, 6.35) * mm, "end": v(12.7, 7.62) * mm});
            skLineSegment(sketch, "E1.9.5.1", {"start": v(11.43, 6.35) * mm, "end": v(11.43, 7.62) * mm});
            skLineSegment(sketch, "E1.9.5.2", {"start": v(11.43, 7.62) * mm, "end": v(12.7, 7.62) * mm});
            skLineSegment(sketch, "E1.9.5.3", {"start": v(11.43, 6.35) * mm, "end": v(12.7, 6.35) * mm});
            skLineSegment(sketch, "E1.9.6.0", {"start": v(12.7, 7.62) * mm, "end": v(12.7, 8.9) * mm});
            skLineSegment(sketch, "E1.9.6.1", {"start": v(11.43, 7.62) * mm, "end": v(11.43, 8.9) * mm});
            skLineSegment(sketch, "E1.9.6.2", {"start": v(11.43, 8.9) * mm, "end": v(12.7, 8.9) * mm});
            skLineSegment(sketch, "E1.9.6.3", {"start": v(11.43, 7.62) * mm, "end": v(12.7, 7.62) * mm});
            skLineSegment(sketch, "E1.9.7.0", {"start": v(12.7, 8.9) * mm, "end": v(12.7, 10.16) * mm});
            skLineSegment(sketch, "E1.9.7.1", {"start": v(11.43, 8.9) * mm, "end": v(11.43, 10.16) * mm});
            skLineSegment(sketch, "E1.9.7.2", {"start": v(11.43, 10.16) * mm, "end": v(12.7, 10.16) * mm});
            skLineSegment(sketch, "E1.9.7.3", {"start": v(11.43, 8.89) * mm, "end": v(12.7, 8.89) * mm});
            skLineSegment(sketch, "E1.9.8.0", {"start": v(12.7, 10.16) * mm, "end": v(12.7, 11.43) * mm});
            skLineSegment(sketch, "E1.9.8.1", {"start": v(11.43, 10.16) * mm, "end": v(11.43, 11.43) * mm});
            skLineSegment(sketch, "E1.9.8.2", {"start": v(11.43, 11.43) * mm, "end": v(12.7, 11.43) * mm});
            skLineSegment(sketch, "E1.9.8.3", {"start": v(11.43, 10.16) * mm, "end": v(12.7, 10.16) * mm});
            skLineSegment(sketch, "E1.9.9.0", {"start": v(12.7, 11.43) * mm, "end": v(12.7, 12.7) * mm});
            skLineSegment(sketch, "E1.9.9.1", {"start": v(11.43, 11.43) * mm, "end": v(11.43, 12.7) * mm});
            skLineSegment(sketch, "E1.9.9.2", {"start": v(11.43, 12.7) * mm, "end": v(12.7, 12.7) * mm});
            skLineSegment(sketch, "E1.9.9.3", {"start": v(11.43, 11.43) * mm, "end": v(12.7, 11.43) * mm});
            skLineSegment(sketch, "E1.direction1", {"start": v(0, 0) * mm, "end": v(1.27, 0) * mm, "construction": true});
            skLineSegment(sketch, "E1.direction2", {"start": v(0, 0) * mm, "end": v(0, 1.27) * mm, "construction": true});
            skSolve(sketch);
        }
        {
            var Q0;
            Q0=makeQuery(id+"F0.imprint","IMPRINT",FACE,{"disambiguationData":[TD([[makeQuery(id+"F0.imprint","IMPRINT",EDGE,{"derivedFrom":sQuery(id+"F0.wireOp",EDGE,"E1.0.9.1")}),-1.0]])]});
            var Q1;
            Q1=makeQuery(id+"F0.imprint","IMPRINT",FACE,{"disambiguationData":[TD([[makeQuery(id+"F0.imprint","IMPRINT",EDGE,{"derivedFrom":sQuery(id+"F0.wireOp",EDGE,"E1.1.8.1")}),-1.0]])]});
            var Q2;
            Q2=makeQuery(id+"F0.imprint","IMPRINT",FACE,{"disambiguationData":[TD([[makeQuery(id+"F0.imprint","IMPRINT",EDGE,{"derivedFrom":sQuery(id+"F0.wireOp",EDGE,"E1.2.9.1")}),-1.0]])]});
            var Q3;
            Q3=makeQuery(id+"F0.imprint","IMPRINT",FACE,{"disambiguationData":[TD([[makeQuery(id+"F0.imprint","IMPRINT",EDGE,{"derivedFrom":sQuery(id+"F0.wireOp",EDGE,"E1.3.8.1")}),-1.0]])]});
            var Q4;
            Q4=makeQuery(id+"F0.imprint","IMPRINT",FACE,{"disambiguationData":[TD([[makeQuery(id+"F0.imprint","IMPRINT",EDGE,{"derivedFrom":sQuery(id+"F0.wireOp",EDGE,"E1.4.9.1")}),-1.0]])]});
            var Q5;
            Q5=makeQuery(id+"F0.imprint","IMPRINT",FACE,{"disambiguationData":[TD([[makeQuery(id+"F0.imprint","IMPRINT",EDGE,{"derivedFrom":sQuery(id+"F0.wireOp",EDGE,"E1.5.8.1")}),-1.0]])]});
            var Q6;
            Q6=makeQuery(id+"F0.imprint","IMPRINT",FACE,{"disambiguationData":[TD([[makeQuery(id+"F0.imprint","IMPRINT",EDGE,{"derivedFrom":sQuery(id+"F0.wireOp",EDGE,"E1.6.9.1")}),-1.0]])]});
            var Q7;
            Q7=makeQuery(id+"F0.imprint","IMPRINT",FACE,{"disambiguationData":[TD([[makeQuery(id+"F0.imprint","IMPRINT",EDGE,{"derivedFrom":sQuery(id+"F0.wireOp",EDGE,"E1.7.8.1")}),-1.0]])]});
            var Q8;
            Q8=makeQuery(id+"F0.imprint","IMPRINT",FACE,{"disambiguationData":[TD([[makeQuery(id+"F0.imprint","IMPRINT",EDGE,{"derivedFrom":sQuery(id+"F0.wireOp",EDGE,"E1.8.9.1")}),-1.0]])]});
            var Q9;
            Q9=makeQuery(id+"F0.imprint","IMPRINT",FACE,{"disambiguationData":[TD([[makeQuery(id+"F0.imprint","IMPRINT",EDGE,{"derivedFrom":sQuery(id+"F0.wireOp",EDGE,"E1.9.8.0")}),1.0]])]});
            var Q10;
            Q10=makeQuery(id+"F0.imprint","IMPRINT",FACE,{"disambiguationData":[TD([[makeQuery(id+"F0.imprint","IMPRINT",EDGE,{"derivedFrom":sQuery(id+"F0.wireOp",EDGE,"E1.8.7.1")}),-1.0]])]});
            var Q11;
            Q11=makeQuery(id+"F0.imprint","IMPRINT",FACE,{"disambiguationData":[TD([[makeQuery(id+"F0.imprint","IMPRINT",EDGE,{"derivedFrom":sQuery(id+"F0.wireOp",EDGE,"E1.6.7.1")}),-1.0]])]});
            var Q12;
            Q12=makeQuery(id+"F0.imprint","IMPRINT",FACE,{"disambiguationData":[TD([[makeQuery(id+"F0.imprint","IMPRINT",EDGE,{"derivedFrom":sQuery(id+"F0.wireOp",EDGE,"E1.4.7.1")}),-1.0]])]});
            var Q13;
            Q13=makeQuery(id+"F0.imprint","IMPRINT",FACE,{"disambiguationData":[TD([[makeQuery(id+"F0.imprint","IMPRINT",EDGE,{"derivedFrom":sQuery(id+"F0.wireOp",EDGE,"E1.2.7.1")}),-1.0]])]});
            var Q14;
            Q14=makeQuery(id+"F0.imprint","IMPRINT",FACE,{"disambiguationData":[TD([[makeQuery(id+"F0.imprint","IMPRINT",EDGE,{"derivedFrom":sQuery(id+"F0.wireOp",EDGE,"E1.0.7.1")}),-1.0]])]});
            var Q15;
            Q15=makeQuery(id+"F0.imprint","IMPRINT",FACE,{"disambiguationData":[TD([[makeQuery(id+"F0.imprint","IMPRINT",EDGE,{"derivedFrom":sQuery(id+"F0.wireOp",EDGE,"E1.1.6.1")}),-1.0]])]});
            var Q16;
            Q16=makeQuery(id+"F0.imprint","IMPRINT",FACE,{"disambiguationData":[TD([[makeQuery(id+"F0.imprint","IMPRINT",EDGE,{"derivedFrom":sQuery(id+"F0.wireOp",EDGE,"E1.3.6.1")}),-1.0]])]});
            var Q17;
            Q17=makeQuery(id+"F0.imprint","IMPRINT",FACE,{"disambiguationData":[TD([[makeQuery(id+"F0.imprint","IMPRINT",EDGE,{"derivedFrom":sQuery(id+"F0.wireOp",EDGE,"E1.5.6.1")}),-1.0]])]});
            var Q18;
            Q18=makeQuery(id+"F0.imprint","IMPRINT",FACE,{"disambiguationData":[TD([[makeQuery(id+"F0.imprint","IMPRINT",EDGE,{"derivedFrom":sQuery(id+"F0.wireOp",EDGE,"E1.7.6.1")}),-1.0]])]});
            var Q19;
            Q19=makeQuery(id+"F0.imprint","IMPRINT",FACE,{"disambiguationData":[TD([[makeQuery(id+"F0.imprint","IMPRINT",EDGE,{"derivedFrom":sQuery(id+"F0.wireOp",EDGE,"E1.9.6.0")}),1.0]])]});
            var Q20;
            Q20=makeQuery(id+"F0.imprint","IMPRINT",FACE,{"disambiguationData":[TD([[makeQuery(id+"F0.imprint","IMPRINT",EDGE,{"derivedFrom":sQuery(id+"F0.wireOp",EDGE,"E1.8.5.1")}),-1.0]])]});
            var Q21;
            Q21=makeQuery(id+"F0.imprint","IMPRINT",FACE,{"disambiguationData":[TD([[makeQuery(id+"F0.imprint","IMPRINT",EDGE,{"derivedFrom":sQuery(id+"F0.wireOp",EDGE,"E1.6.5.1")}),-1.0]])]});
            var Q22;
            Q22=makeQuery(id+"F0.imprint","IMPRINT",FACE,{"disambiguationData":[TD([[makeQuery(id+"F0.imprint","IMPRINT",EDGE,{"derivedFrom":sQuery(id+"F0.wireOp",EDGE,"E1.4.5.1")}),-1.0]])]});
            var Q23;
            Q23=makeQuery(id+"F0.imprint","IMPRINT",FACE,{"disambiguationData":[TD([[makeQuery(id+"F0.imprint","IMPRINT",EDGE,{"derivedFrom":sQuery(id+"F0.wireOp",EDGE,"E1.2.5.1")}),-1.0]])]});
            var Q24;
            Q24=makeQuery(id+"F0.imprint","IMPRINT",FACE,{"disambiguationData":[TD([[makeQuery(id+"F0.imprint","IMPRINT",EDGE,{"derivedFrom":sQuery(id+"F0.wireOp",EDGE,"E1.0.5.1")}),-1.0]])]});
            var Q25;
            Q25=makeQuery(id+"F0.imprint","IMPRINT",FACE,{"disambiguationData":[TD([[makeQuery(id+"F0.imprint","IMPRINT",EDGE,{"derivedFrom":sQuery(id+"F0.wireOp",EDGE,"E1.1.4.1")}),-1.0]])]});
            var Q26;
            Q26=makeQuery(id+"F0.imprint","IMPRINT",FACE,{"disambiguationData":[TD([[makeQuery(id+"F0.imprint","IMPRINT",EDGE,{"derivedFrom":sQuery(id+"F0.wireOp",EDGE,"E1.3.4.1")}),-1.0]])]});
            var Q27;
            Q27=makeQuery(id+"F0.imprint","IMPRINT",FACE,{"disambiguationData":[TD([[makeQuery(id+"F0.imprint","IMPRINT",EDGE,{"derivedFrom":sQuery(id+"F0.wireOp",EDGE,"E1.5.4.1")}),-1.0]])]});
            var Q28;
            Q28=makeQuery(id+"F0.imprint","IMPRINT",FACE,{"disambiguationData":[TD([[makeQuery(id+"F0.imprint","IMPRINT",EDGE,{"derivedFrom":sQuery(id+"F0.wireOp",EDGE,"E1.7.4.1")}),-1.0]])]});
            var Q29;
            Q29=makeQuery(id+"F0.imprint","IMPRINT",FACE,{"disambiguationData":[TD([[makeQuery(id+"F0.imprint","IMPRINT",EDGE,{"derivedFrom":sQuery(id+"F0.wireOp",EDGE,"E1.9.4.0")}),1.0]])]});
            var Q30;
            Q30=makeQuery(id+"F0.imprint","IMPRINT",FACE,{"disambiguationData":[TD([[makeQuery(id+"F0.imprint","IMPRINT",EDGE,{"derivedFrom":sQuery(id+"F0.wireOp",EDGE,"E1.8.3.1")}),-1.0]])]});
            var Q31;
            Q31=makeQuery(id+"F0.imprint","IMPRINT",FACE,{"disambiguationData":[TD([[makeQuery(id+"F0.imprint","IMPRINT",EDGE,{"derivedFrom":sQuery(id+"F0.wireOp",EDGE,"E1.6.3.1")}),-1.0]])]});
            var Q32;
            Q32=makeQuery(id+"F0.imprint","IMPRINT",FACE,{"disambiguationData":[TD([[makeQuery(id+"F0.imprint","IMPRINT",EDGE,{"derivedFrom":sQuery(id+"F0.wireOp",EDGE,"E1.4.3.1")}),-1.0]])]});
            var Q33;
            Q33=makeQuery(id+"F0.imprint","IMPRINT",FACE,{"disambiguationData":[TD([[makeQuery(id+"F0.imprint","IMPRINT",EDGE,{"derivedFrom":sQuery(id+"F0.wireOp",EDGE,"E1.2.3.1")}),-1.0]])]});
            var Q34;
            Q34=makeQuery(id+"F0.imprint","IMPRINT",FACE,{"disambiguationData":[TD([[makeQuery(id+"F0.imprint","IMPRINT",EDGE,{"derivedFrom":sQuery(id+"F0.wireOp",EDGE,"E1.0.3.1")}),-1.0]])]});
            var Q35;
            Q35=makeQuery(id+"F0.imprint","IMPRINT",FACE,{"disambiguationData":[TD([[makeQuery(id+"F0.imprint","IMPRINT",EDGE,{"derivedFrom":sQuery(id+"F0.wireOp",EDGE,"E1.1.2.1")}),-1.0]])]});
            var Q36;
            Q36=makeQuery(id+"F0.imprint","IMPRINT",FACE,{"disambiguationData":[TD([[makeQuery(id+"F0.imprint","IMPRINT",EDGE,{"derivedFrom":sQuery(id+"F0.wireOp",EDGE,"E1.3.2.1")}),-1.0]])]});
            var Q37;
            Q37=makeQuery(id+"F0.imprint","IMPRINT",FACE,{"disambiguationData":[TD([[makeQuery(id+"F0.imprint","IMPRINT",EDGE,{"derivedFrom":sQuery(id+"F0.wireOp",EDGE,"E1.5.2.1")}),-1.0]])]});
            var Q38;
            Q38=makeQuery(id+"F0.imprint","IMPRINT",FACE,{"disambiguationData":[TD([[makeQuery(id+"F0.imprint","IMPRINT",EDGE,{"derivedFrom":sQuery(id+"F0.wireOp",EDGE,"E1.7.2.1")}),-1.0]])]});
            var Q39;
            Q39=makeQuery(id+"F0.imprint","IMPRINT",FACE,{"disambiguationData":[TD([[makeQuery(id+"F0.imprint","IMPRINT",EDGE,{"derivedFrom":sQuery(id+"F0.wireOp",EDGE,"E1.9.2.0")}),1.0]])]});
            var Q40;
            Q40=makeQuery(id+"F0.imprint","IMPRINT",FACE,{"disambiguationData":[TD([[makeQuery(id+"F0.imprint","IMPRINT",EDGE,{"derivedFrom":sQuery(id+"F0.wireOp",EDGE,"E1.8.1.1")}),-1.0]])]});
            var Q41;
            Q41=makeQuery(id+"F0.imprint","IMPRINT",FACE,{"disambiguationData":[TD([[makeQuery(id+"F0.imprint","IMPRINT",EDGE,{"derivedFrom":sQuery(id+"F0.wireOp",EDGE,"E1.6.1.1")}),-1.0]])]});
            var Q42;
            Q42=makeQuery(id+"F0.imprint","IMPRINT",FACE,{"disambiguationData":[TD([[makeQuery(id+"F0.imprint","IMPRINT",EDGE,{"derivedFrom":sQuery(id+"F0.wireOp",EDGE,"E1.4.1.1")}),-1.0]])]});
            var Q43;
            Q43=makeQuery(id+"F0.imprint","IMPRINT",FACE,{"disambiguationData":[TD([[makeQuery(id+"F0.imprint","IMPRINT",EDGE,{"derivedFrom":sQuery(id+"F0.wireOp",EDGE,"E1.2.1.1")}),-1.0]])]});
            var Q44;
            Q44=makeQuery(id+"F0.imprint","IMPRINT",FACE,{"disambiguationData":[TD([[makeQuery(id+"F0.imprint","IMPRINT",EDGE,{"derivedFrom":sQuery(id+"F0.wireOp",EDGE,"E1.0.1.1")}),-1.0]])]});
            var Q45;
            Q45=makeQuery(id+"F0.imprint","IMPRINT",FACE,{"disambiguationData":[TD([[makeQuery(id+"F0.imprint","IMPRINT",EDGE,{"derivedFrom":sQuery(id+"F0.wireOp",EDGE,"E0.right")}),-1.0]])]});
            var Q46;
            Q46=makeQuery(id+"F0.imprint","IMPRINT",FACE,{"disambiguationData":[TD([[makeQuery(id+"F0.imprint","IMPRINT",EDGE,{"derivedFrom":sQuery(id+"F0.wireOp",EDGE,"E1.3.0.1")}),-1.0]])]});
            var Q47;
            Q47=makeQuery(id+"F0.imprint","IMPRINT",FACE,{"disambiguationData":[TD([[makeQuery(id+"F0.imprint","IMPRINT",EDGE,{"derivedFrom":sQuery(id+"F0.wireOp",EDGE,"E1.5.0.1")}),-1.0]])]});
            var Q48;
            Q48=makeQuery(id+"F0.imprint","IMPRINT",FACE,{"disambiguationData":[TD([[makeQuery(id+"F0.imprint","IMPRINT",EDGE,{"derivedFrom":sQuery(id+"F0.wireOp",EDGE,"E1.7.0.1")}),-1.0]])]});
            var Q49;
            Q49=makeQuery(id+"F0.imprint","IMPRINT",FACE,{"disambiguationData":[TD([[makeQuery(id+"F0.imprint","IMPRINT",EDGE,{"derivedFrom":sQuery(id+"F0.wireOp",EDGE,"E1.9.0.0")}),1.0]])]});
            extrude(context, id + "F1", {"entities" : qUnion([Q0, Q1, Q2, Q3, Q4, Q5, Q6, Q7, Q8, Q9, Q10, Q11, Q12, Q13, Q14, Q15, Q16, Q17, Q18, Q19, Q20, Q21, Q22, Q23, Q24, Q25, Q26, Q27, Q28, Q29, Q30, Q31, Q32, Q33, Q34, Q35, Q36, Q37, Q38, Q39, Q40, Q41, Q42, Q43, Q44, Q45, Q46, Q47, Q48, Q49]), "depth" : 1.27 * mm});
        }
        {
            var Q0;
            Q0=makeQuery(id+"F1.opExtrude","CAP_EDGE",EDGE,{"disambiguationData":[OSD([sQuery(id+"F0.wireOp",EDGE,"E1.0.9.2")])],"isStart":false});
            var Q1;
            Q1=makeQuery(id+"F1.opExtrude","CAP_FACE",FACE,{"disambiguationData":[OSD([sQuery(id+"F0.wireOp",EDGE,"E1.0.9.1"),sQuery(id+"F0.wireOp",EDGE,"E1.0.9.2"),sQuery(id+"F0.wireOp",EDGE,"E1.0.9.3"),sQuery(id+"F0.wireOp",EDGE,"E1.1.9.1")])],"isStart":false});
            var Q2;
            Q2=makeQuery(id+"F1.opExtrude","CAP_FACE",FACE,{"disambiguationData":[OSD([sQuery(id+"F0.wireOp",EDGE,"E1.2.9.1"),sQuery(id+"F0.wireOp",EDGE,"E1.2.9.2"),sQuery(id+"F0.wireOp",EDGE,"E1.2.9.3"),sQuery(id+"F0.wireOp",EDGE,"E1.3.9.1")])],"isStart":false});
            var Q3;
            Q3=makeQuery(id+"F1.opExtrude","CAP_FACE",FACE,{"disambiguationData":[OSD([sQuery(id+"F0.wireOp",EDGE,"E1.4.9.1"),sQuery(id+"F0.wireOp",EDGE,"E1.4.9.2"),sQuery(id+"F0.wireOp",EDGE,"E1.4.9.3"),sQuery(id+"F0.wireOp",EDGE,"E1.5.9.1")])],"isStart":false});
            var Q4;
            Q4=makeQuery(id+"F1.opExtrude","CAP_FACE",FACE,{"disambiguationData":[OSD([sQuery(id+"F0.wireOp",EDGE,"E1.6.9.1"),sQuery(id+"F0.wireOp",EDGE,"E1.6.9.2"),sQuery(id+"F0.wireOp",EDGE,"E1.6.9.3"),sQuery(id+"F0.wireOp",EDGE,"E1.7.9.1")])],"isStart":false});
            var Q5;
            Q5=makeQuery(id+"F1.opExtrude","CAP_FACE",FACE,{"disambiguationData":[OSD([sQuery(id+"F0.wireOp",EDGE,"E1.8.9.1"),sQuery(id+"F0.wireOp",EDGE,"E1.8.9.2"),sQuery(id+"F0.wireOp",EDGE,"E1.8.9.3"),sQuery(id+"F0.wireOp",EDGE,"E1.9.9.1")])],"isStart":false});
            var Q6;
            Q6=makeQuery(id+"F1.opExtrude","CAP_FACE",FACE,{"disambiguationData":[OSD([sQuery(id+"F0.wireOp",EDGE,"E1.9.8.0"),sQuery(id+"F0.wireOp",EDGE,"E1.9.8.1"),sQuery(id+"F0.wireOp",EDGE,"E1.9.8.3"),sQuery(id+"F0.wireOp",EDGE,"E1.9.9.3")])],"isStart":false});
            var Q7;
            Q7=makeQuery(id+"F1.opExtrude","CAP_FACE",FACE,{"disambiguationData":[OSD([sQuery(id+"F0.wireOp",EDGE,"E1.7.8.1"),sQuery(id+"F0.wireOp",EDGE,"E1.7.8.3"),sQuery(id+"F0.wireOp",EDGE,"E1.7.9.3"),sQuery(id+"F0.wireOp",EDGE,"E1.8.8.1")])],"isStart":false});
            var Q8;
            Q8=makeQuery(id+"F1.opExtrude","CAP_FACE",FACE,{"disambiguationData":[OSD([sQuery(id+"F0.wireOp",EDGE,"E1.5.8.1"),sQuery(id+"F0.wireOp",EDGE,"E1.5.8.3"),sQuery(id+"F0.wireOp",EDGE,"E1.5.9.3"),sQuery(id+"F0.wireOp",EDGE,"E1.6.8.1")])],"isStart":false});
            var Q9;
            Q9=makeQuery(id+"F1.opExtrude","CAP_FACE",FACE,{"disambiguationData":[OSD([sQuery(id+"F0.wireOp",EDGE,"E1.3.8.1"),sQuery(id+"F0.wireOp",EDGE,"E1.3.8.3"),sQuery(id+"F0.wireOp",EDGE,"E1.3.9.3"),sQuery(id+"F0.wireOp",EDGE,"E1.4.8.1")])],"isStart":false});
            var Q10;
            Q10=makeQuery(id+"F1.opExtrude","CAP_FACE",FACE,{"disambiguationData":[OSD([sQuery(id+"F0.wireOp",EDGE,"E1.1.8.1"),sQuery(id+"F0.wireOp",EDGE,"E1.1.8.3"),sQuery(id+"F0.wireOp",EDGE,"E1.1.9.3"),sQuery(id+"F0.wireOp",EDGE,"E1.2.8.1")])],"isStart":false});
            var Q11;
            Q11=makeQuery(id+"F1.opExtrude","CAP_FACE",FACE,{"disambiguationData":[OSD([sQuery(id+"F0.wireOp",EDGE,"E1.0.7.1"),sQuery(id+"F0.wireOp",EDGE,"E1.0.7.3"),sQuery(id+"F0.wireOp",EDGE,"E1.0.8.3"),sQuery(id+"F0.wireOp",EDGE,"E1.1.7.1")])],"isStart":false});
            var Q12;
            Q12=makeQuery(id+"F1.opExtrude","CAP_FACE",FACE,{"disambiguationData":[OSD([sQuery(id+"F0.wireOp",EDGE,"E1.2.7.1"),sQuery(id+"F0.wireOp",EDGE,"E1.2.7.3"),sQuery(id+"F0.wireOp",EDGE,"E1.2.8.3"),sQuery(id+"F0.wireOp",EDGE,"E1.3.7.1")])],"isStart":false});
            var Q13;
            Q13=makeQuery(id+"F1.opExtrude","CAP_FACE",FACE,{"disambiguationData":[OSD([sQuery(id+"F0.wireOp",EDGE,"E1.1.6.1"),sQuery(id+"F0.wireOp",EDGE,"E1.1.6.3"),sQuery(id+"F0.wireOp",EDGE,"E1.1.7.3"),sQuery(id+"F0.wireOp",EDGE,"E1.2.6.1")])],"isStart":false});
            var Q14;
            Q14=makeQuery(id+"F1.opExtrude","CAP_FACE",FACE,{"disambiguationData":[OSD([sQuery(id+"F0.wireOp",EDGE,"E1.0.5.1"),sQuery(id+"F0.wireOp",EDGE,"E1.0.5.3"),sQuery(id+"F0.wireOp",EDGE,"E1.0.6.3"),sQuery(id+"F0.wireOp",EDGE,"E1.1.5.1")])],"isStart":false});
            var Q15;
            Q15=makeQuery(id+"F1.opExtrude","CAP_FACE",FACE,{"disambiguationData":[OSD([sQuery(id+"F0.wireOp",EDGE,"E1.2.5.1"),sQuery(id+"F0.wireOp",EDGE,"E1.2.5.3"),sQuery(id+"F0.wireOp",EDGE,"E1.2.6.3"),sQuery(id+"F0.wireOp",EDGE,"E1.3.5.1")])],"isStart":false});
            var Q16;
            Q16=makeQuery(id+"F1.opExtrude","CAP_FACE",FACE,{"disambiguationData":[OSD([sQuery(id+"F0.wireOp",EDGE,"E1.3.6.1"),sQuery(id+"F0.wireOp",EDGE,"E1.3.6.3"),sQuery(id+"F0.wireOp",EDGE,"E1.3.7.3"),sQuery(id+"F0.wireOp",EDGE,"E1.4.6.1")])],"isStart":false});
            var Q17;
            Q17=makeQuery(id+"F1.opExtrude","CAP_FACE",FACE,{"disambiguationData":[OSD([sQuery(id+"F0.wireOp",EDGE,"E1.4.7.1"),sQuery(id+"F0.wireOp",EDGE,"E1.4.7.3"),sQuery(id+"F0.wireOp",EDGE,"E1.4.8.3"),sQuery(id+"F0.wireOp",EDGE,"E1.5.7.1")])],"isStart":false});
            var Q18;
            Q18=makeQuery(id+"F1.opExtrude","CAP_FACE",FACE,{"disambiguationData":[OSD([sQuery(id+"F0.wireOp",EDGE,"E1.5.6.1"),sQuery(id+"F0.wireOp",EDGE,"E1.5.6.3"),sQuery(id+"F0.wireOp",EDGE,"E1.5.7.3"),sQuery(id+"F0.wireOp",EDGE,"E1.6.6.1")])],"isStart":false});
            var Q19;
            Q19=makeQuery(id+"F1.opExtrude","CAP_FACE",FACE,{"disambiguationData":[OSD([sQuery(id+"F0.wireOp",EDGE,"E1.6.7.1"),sQuery(id+"F0.wireOp",EDGE,"E1.6.7.3"),sQuery(id+"F0.wireOp",EDGE,"E1.6.8.3"),sQuery(id+"F0.wireOp",EDGE,"E1.7.7.1")])],"isStart":false});
            var Q20;
            Q20=makeQuery(id+"F1.opExtrude","CAP_FACE",FACE,{"disambiguationData":[OSD([sQuery(id+"F0.wireOp",EDGE,"E1.7.6.1"),sQuery(id+"F0.wireOp",EDGE,"E1.7.6.3"),sQuery(id+"F0.wireOp",EDGE,"E1.7.7.3"),sQuery(id+"F0.wireOp",EDGE,"E1.8.6.1")])],"isStart":false});
            var Q21;
            Q21=makeQuery(id+"F1.opExtrude","CAP_FACE",FACE,{"disambiguationData":[OSD([sQuery(id+"F0.wireOp",EDGE,"E1.8.7.1"),sQuery(id+"F0.wireOp",EDGE,"E1.8.7.3"),sQuery(id+"F0.wireOp",EDGE,"E1.8.8.3"),sQuery(id+"F0.wireOp",EDGE,"E1.9.7.1")])],"isStart":false});
            var Q22;
            Q22=makeQuery(id+"F1.opExtrude","CAP_FACE",FACE,{"disambiguationData":[OSD([sQuery(id+"F0.wireOp",EDGE,"E1.9.6.0"),sQuery(id+"F0.wireOp",EDGE,"E1.9.6.1"),sQuery(id+"F0.wireOp",EDGE,"E1.9.6.3"),sQuery(id+"F0.wireOp",EDGE,"E1.9.7.3")])],"isStart":false});
            var Q23;
            Q23=makeQuery(id+"F1.opExtrude","CAP_FACE",FACE,{"disambiguationData":[OSD([sQuery(id+"F0.wireOp",EDGE,"E1.8.5.1"),sQuery(id+"F0.wireOp",EDGE,"E1.8.5.3"),sQuery(id+"F0.wireOp",EDGE,"E1.8.6.3"),sQuery(id+"F0.wireOp",EDGE,"E1.9.5.1")])],"isStart":false});
            var Q24;
            Q24=makeQuery(id+"F1.opExtrude","CAP_FACE",FACE,{"disambiguationData":[OSD([sQuery(id+"F0.wireOp",EDGE,"E1.6.5.1"),sQuery(id+"F0.wireOp",EDGE,"E1.6.5.3"),sQuery(id+"F0.wireOp",EDGE,"E1.6.6.3"),sQuery(id+"F0.wireOp",EDGE,"E1.7.5.1")])],"isStart":false});
            var Q25;
            Q25=makeQuery(id+"F1.opExtrude","CAP_FACE",FACE,{"disambiguationData":[OSD([sQuery(id+"F0.wireOp",EDGE,"E1.4.5.1"),sQuery(id+"F0.wireOp",EDGE,"E1.4.5.3"),sQuery(id+"F0.wireOp",EDGE,"E1.4.6.3"),sQuery(id+"F0.wireOp",EDGE,"E1.5.5.1")])],"isStart":false});
            var Q26;
            Q26=makeQuery(id+"F1.opExtrude","CAP_FACE",FACE,{"disambiguationData":[OSD([sQuery(id+"F0.wireOp",EDGE,"E1.3.4.1"),sQuery(id+"F0.wireOp",EDGE,"E1.3.4.3"),sQuery(id+"F0.wireOp",EDGE,"E1.3.5.3"),sQuery(id+"F0.wireOp",EDGE,"E1.4.4.1")])],"isStart":false});
            var Q27;
            Q27=makeQuery(id+"F1.opExtrude","CAP_FACE",FACE,{"disambiguationData":[OSD([sQuery(id+"F0.wireOp",EDGE,"E1.1.4.1"),sQuery(id+"F0.wireOp",EDGE,"E1.1.4.3"),sQuery(id+"F0.wireOp",EDGE,"E1.1.5.3"),sQuery(id+"F0.wireOp",EDGE,"E1.2.4.1")])],"isStart":false});
            var Q28;
            Q28=makeQuery(id+"F1.opExtrude","CAP_FACE",FACE,{"disambiguationData":[OSD([sQuery(id+"F0.wireOp",EDGE,"E1.2.3.1"),sQuery(id+"F0.wireOp",EDGE,"E1.2.3.3"),sQuery(id+"F0.wireOp",EDGE,"E1.2.4.3"),sQuery(id+"F0.wireOp",EDGE,"E1.3.3.1")])],"isStart":false});
            var Q29;
            Q29=makeQuery(id+"F1.opExtrude","CAP_FACE",FACE,{"disambiguationData":[OSD([sQuery(id+"F0.wireOp",EDGE,"E1.1.2.1"),sQuery(id+"F0.wireOp",EDGE,"E1.1.2.3"),sQuery(id+"F0.wireOp",EDGE,"E1.1.3.3"),sQuery(id+"F0.wireOp",EDGE,"E1.2.2.1")])],"isStart":false});
            var Q30;
            Q30=makeQuery(id+"F1.opExtrude","CAP_EDGE",EDGE,{"disambiguationData":[OSD([sQuery(id+"F0.wireOp",EDGE,"E0.top")])],"isStart":false});
            var Q31;
            Q31=makeQuery(id+"F1.opExtrude","CAP_FACE",FACE,{"disambiguationData":[OSD([sQuery(id+"F0.wireOp",EDGE,"E0.right"),sQuery(id+"F0.wireOp",EDGE,"E1.1.0.3"),sQuery(id+"F0.wireOp",EDGE,"E1.1.1.3"),sQuery(id+"F0.wireOp",EDGE,"E1.2.0.1")])],"isStart":false});
            var Q32;
            Q32=makeQuery(id+"F1.opExtrude","CAP_FACE",FACE,{"disambiguationData":[OSD([sQuery(id+"F0.wireOp",EDGE,"E1.2.1.1"),sQuery(id+"F0.wireOp",EDGE,"E1.2.1.3"),sQuery(id+"F0.wireOp",EDGE,"E1.2.2.3"),sQuery(id+"F0.wireOp",EDGE,"E1.3.1.1")])],"isStart":false});
            var Q33;
            Q33=makeQuery(id+"F1.opExtrude","CAP_FACE",FACE,{"disambiguationData":[OSD([sQuery(id+"F0.wireOp",EDGE,"E1.3.2.1"),sQuery(id+"F0.wireOp",EDGE,"E1.3.2.3"),sQuery(id+"F0.wireOp",EDGE,"E1.3.3.3"),sQuery(id+"F0.wireOp",EDGE,"E1.4.2.1")])],"isStart":false});
            var Q34;
            Q34=makeQuery(id+"F1.opExtrude","CAP_FACE",FACE,{"disambiguationData":[OSD([sQuery(id+"F0.wireOp",EDGE,"E1.3.0.1"),sQuery(id+"F0.wireOp",EDGE,"E1.3.0.3"),sQuery(id+"F0.wireOp",EDGE,"E1.3.1.3"),sQuery(id+"F0.wireOp",EDGE,"E1.4.0.1")])],"isStart":false});
            var Q35;
            Q35=makeQuery(id+"F1.opExtrude","CAP_FACE",FACE,{"disambiguationData":[OSD([sQuery(id+"F0.wireOp",EDGE,"E1.4.1.1"),sQuery(id+"F0.wireOp",EDGE,"E1.4.1.3"),sQuery(id+"F0.wireOp",EDGE,"E1.4.2.3"),sQuery(id+"F0.wireOp",EDGE,"E1.5.1.1")])],"isStart":false});
            var Q36;
            Q36=makeQuery(id+"F1.opExtrude","CAP_FACE",FACE,{"disambiguationData":[OSD([sQuery(id+"F0.wireOp",EDGE,"E1.4.3.1"),sQuery(id+"F0.wireOp",EDGE,"E1.4.3.3"),sQuery(id+"F0.wireOp",EDGE,"E1.4.4.3"),sQuery(id+"F0.wireOp",EDGE,"E1.5.3.1")])],"isStart":false});
            var Q37;
            Q37=makeQuery(id+"F1.opExtrude","CAP_FACE",FACE,{"disambiguationData":[OSD([sQuery(id+"F0.wireOp",EDGE,"E1.5.0.1"),sQuery(id+"F0.wireOp",EDGE,"E1.5.0.3"),sQuery(id+"F0.wireOp",EDGE,"E1.5.1.3"),sQuery(id+"F0.wireOp",EDGE,"E1.6.0.1")])],"isStart":false});
            var Q38;
            Q38=makeQuery(id+"F1.opExtrude","CAP_FACE",FACE,{"disambiguationData":[OSD([sQuery(id+"F0.wireOp",EDGE,"E1.0.1.1"),sQuery(id+"F0.wireOp",EDGE,"E0.top"),sQuery(id+"F0.wireOp",EDGE,"E1.0.2.3"),sQuery(id+"F0.wireOp",EDGE,"E1.1.1.1")])],"isStart":false});
            var Q39;
            Q39=makeQuery(id+"F1.opExtrude","CAP_FACE",FACE,{"disambiguationData":[OSD([sQuery(id+"F0.wireOp",EDGE,"E1.0.3.1"),sQuery(id+"F0.wireOp",EDGE,"E1.0.3.3"),sQuery(id+"F0.wireOp",EDGE,"E1.0.4.3"),sQuery(id+"F0.wireOp",EDGE,"E1.1.3.1")])],"isStart":false});
            var Q40;
            Q40=makeQuery(id+"F1.opExtrude","CAP_FACE",FACE,{"disambiguationData":[OSD([sQuery(id+"F0.wireOp",EDGE,"E1.5.2.1"),sQuery(id+"F0.wireOp",EDGE,"E1.5.2.3"),sQuery(id+"F0.wireOp",EDGE,"E1.5.3.3"),sQuery(id+"F0.wireOp",EDGE,"E1.6.2.1")])],"isStart":false});
            var Q41;
            Q41=makeQuery(id+"F1.opExtrude","CAP_FACE",FACE,{"disambiguationData":[OSD([sQuery(id+"F0.wireOp",EDGE,"E1.5.4.1"),sQuery(id+"F0.wireOp",EDGE,"E1.5.4.3"),sQuery(id+"F0.wireOp",EDGE,"E1.5.5.3"),sQuery(id+"F0.wireOp",EDGE,"E1.6.4.1")])],"isStart":false});
            var Q42;
            Q42=makeQuery(id+"F1.opExtrude","CAP_FACE",FACE,{"disambiguationData":[OSD([sQuery(id+"F0.wireOp",EDGE,"E1.6.3.1"),sQuery(id+"F0.wireOp",EDGE,"E1.6.3.3"),sQuery(id+"F0.wireOp",EDGE,"E1.6.4.3"),sQuery(id+"F0.wireOp",EDGE,"E1.7.3.1")])],"isStart":false});
            var Q43;
            Q43=makeQuery(id+"F1.opExtrude","CAP_FACE",FACE,{"disambiguationData":[OSD([sQuery(id+"F0.wireOp",EDGE,"E1.6.1.1"),sQuery(id+"F0.wireOp",EDGE,"E1.6.1.3"),sQuery(id+"F0.wireOp",EDGE,"E1.6.2.3"),sQuery(id+"F0.wireOp",EDGE,"E1.7.1.1")])],"isStart":false});
            var Q44;
            Q44=makeQuery(id+"F1.opExtrude","CAP_FACE",FACE,{"disambiguationData":[OSD([sQuery(id+"F0.wireOp",EDGE,"E1.7.2.1"),sQuery(id+"F0.wireOp",EDGE,"E1.7.2.3"),sQuery(id+"F0.wireOp",EDGE,"E1.7.3.3"),sQuery(id+"F0.wireOp",EDGE,"E1.8.2.1")])],"isStart":false});
            var Q45;
            Q45=makeQuery(id+"F1.opExtrude","CAP_FACE",FACE,{"disambiguationData":[OSD([sQuery(id+"F0.wireOp",EDGE,"E1.7.0.1"),sQuery(id+"F0.wireOp",EDGE,"E1.7.0.3"),sQuery(id+"F0.wireOp",EDGE,"E1.7.1.3"),sQuery(id+"F0.wireOp",EDGE,"E1.8.0.1")])],"isStart":false});
            var Q46;
            Q46=makeQuery(id+"F1.opExtrude","CAP_FACE",FACE,{"disambiguationData":[OSD([sQuery(id+"F0.wireOp",EDGE,"E1.8.1.1"),sQuery(id+"F0.wireOp",EDGE,"E1.8.1.3"),sQuery(id+"F0.wireOp",EDGE,"E1.8.2.3"),sQuery(id+"F0.wireOp",EDGE,"E1.9.1.1")])],"isStart":false});
            var Q47;
            Q47=makeQuery(id+"F1.opExtrude","CAP_FACE",FACE,{"disambiguationData":[OSD([sQuery(id+"F0.wireOp",EDGE,"E1.9.0.0"),sQuery(id+"F0.wireOp",EDGE,"E1.9.0.1"),sQuery(id+"F0.wireOp",EDGE,"E1.9.0.3"),sQuery(id+"F0.wireOp",EDGE,"E1.9.1.3")])],"isStart":false});
            var Q48;
            Q48=makeQuery(id+"F1.opExtrude","CAP_FACE",FACE,{"disambiguationData":[OSD([sQuery(id+"F0.wireOp",EDGE,"E1.9.2.0"),sQuery(id+"F0.wireOp",EDGE,"E1.9.2.1"),sQuery(id+"F0.wireOp",EDGE,"E1.9.2.3"),sQuery(id+"F0.wireOp",EDGE,"E1.9.3.3")])],"isStart":false});
            var Q49;
            Q49=makeQuery(id+"F1.opExtrude","CAP_FACE",FACE,{"disambiguationData":[OSD([sQuery(id+"F0.wireOp",EDGE,"E1.8.3.1"),sQuery(id+"F0.wireOp",EDGE,"E1.8.3.3"),sQuery(id+"F0.wireOp",EDGE,"E1.8.4.3"),sQuery(id+"F0.wireOp",EDGE,"E1.9.3.1")])],"isStart":false});
            var Q50;
            Q50=makeQuery(id+"F1.opExtrude","CAP_FACE",FACE,{"disambiguationData":[OSD([sQuery(id+"F0.wireOp",EDGE,"E1.9.4.0"),sQuery(id+"F0.wireOp",EDGE,"E1.9.4.1"),sQuery(id+"F0.wireOp",EDGE,"E1.9.4.3"),sQuery(id+"F0.wireOp",EDGE,"E1.9.5.3")])],"isStart":false});
            var Q51;
            Q51=makeQuery(id+"F1.opExtrude","CAP_FACE",FACE,{"disambiguationData":[OSD([sQuery(id+"F0.wireOp",EDGE,"E1.7.4.1"),sQuery(id+"F0.wireOp",EDGE,"E1.7.4.3"),sQuery(id+"F0.wireOp",EDGE,"E1.7.5.3"),sQuery(id+"F0.wireOp",EDGE,"E1.8.4.1")])],"isStart":false});
            chamfer(context, id + "F2", {"entities" : qUnion([Q0, Q1, Q2, Q3, Q4, Q5, Q6, Q7, Q8, Q9, Q10, Q11, Q12, Q13, Q14, Q15, Q16, Q17, Q18, Q19, Q20, Q21, Q22, Q23, Q24, Q25, Q26, Q27, Q28, Q29, Q30, Q31, Q32, Q33, Q34, Q35, Q36, Q37, Q38, Q39, Q40, Q41, Q42, Q43, Q44, Q45, Q46, Q47, Q48, Q49, Q50, Q51]), "width" : 0.58 * mm, "tangentPropagation" : true});
        }
        {
            var Q0;
            Q0=qCreatedBy(makeId("Top.planeOp"),FACE);
            var sketch = newSketch(context, id + "F3", { "sketchPlane" : qUnion([Q0])});
            skLineSegment(sketch, "E2.bottom", {"start": v(0, 0) * mm, "end": v(1.27, 0) * mm});
            skLineSegment(sketch, "E2.top", {"start": v(0, 1.26) * mm, "end": v(1.27, 1.26) * mm});
            skLineSegment(sketch, "E2.left", {"start": v(0, 0) * mm, "end": v(0, 1.26) * mm});
            skLineSegment(sketch, "E2.right", {"start": v(1.27, 0) * mm, "end": v(1.27, 1.26) * mm});
            skLineSegment(sketch, "E3.0.1.0", {"start": v(1.27, 1.27) * mm, "end": v(1.27, 2.53) * mm});
            skLineSegment(sketch, "E3.0.1.1", {"start": v(0, 1.27) * mm, "end": v(0, 2.53) * mm});
            skLineSegment(sketch, "E3.0.1.2", {"start": v(0, 1.27) * mm, "end": v(1.27, 1.27) * mm});
            skLineSegment(sketch, "E3.0.1.3", {"start": v(0, 2.53) * mm, "end": v(1.27, 2.53) * mm});
            skLineSegment(sketch, "E3.0.2.0", {"start": v(1.27, 2.54) * mm, "end": v(1.27, 3.8) * mm});
            skLineSegment(sketch, "E3.0.2.1", {"start": v(0, 2.54) * mm, "end": v(0, 3.8) * mm});
            skLineSegment(sketch, "E3.0.2.2", {"start": v(0, 2.54) * mm, "end": v(1.27, 2.54) * mm});
            skLineSegment(sketch, "E3.0.2.3", {"start": v(0, 3.8) * mm, "end": v(1.27, 3.8) * mm});
            skLineSegment(sketch, "E3.0.3.0", {"start": v(1.27, 3.81) * mm, "end": v(1.27, 5.07) * mm});
            skLineSegment(sketch, "E3.0.3.1", {"start": v(0, 3.81) * mm, "end": v(0, 5.07) * mm});
            skLineSegment(sketch, "E3.0.3.2", {"start": v(0, 3.81) * mm, "end": v(1.27, 3.81) * mm});
            skLineSegment(sketch, "E3.0.3.3", {"start": v(0, 5.07) * mm, "end": v(1.27, 5.07) * mm});
            skLineSegment(sketch, "E3.0.4.0", {"start": v(1.27, 5.08) * mm, "end": v(1.27, 6.34) * mm});
            skLineSegment(sketch, "E3.0.4.1", {"start": v(0, 5.08) * mm, "end": v(0, 6.34) * mm});
            skLineSegment(sketch, "E3.0.4.2", {"start": v(0, 5.08) * mm, "end": v(1.27, 5.08) * mm});
            skLineSegment(sketch, "E3.0.4.3", {"start": v(0, 6.34) * mm, "end": v(1.27, 6.34) * mm});
            skLineSegment(sketch, "E3.0.5.0", {"start": v(1.27, 6.35) * mm, "end": v(1.27, 7.61) * mm});
            skLineSegment(sketch, "E3.0.5.1", {"start": v(0, 6.35) * mm, "end": v(0, 7.61) * mm});
            skLineSegment(sketch, "E3.0.5.2", {"start": v(0, 6.35) * mm, "end": v(1.27, 6.35) * mm});
            skLineSegment(sketch, "E3.0.5.3", {"start": v(0, 7.61) * mm, "end": v(1.27, 7.61) * mm});
            skLineSegment(sketch, "E3.0.6.0", {"start": v(1.27, 7.62) * mm, "end": v(1.27, 8.88) * mm});
            skLineSegment(sketch, "E3.0.6.1", {"start": v(0, 7.62) * mm, "end": v(0, 8.88) * mm});
            skLineSegment(sketch, "E3.0.6.2", {"start": v(0, 7.62) * mm, "end": v(1.27, 7.62) * mm});
            skLineSegment(sketch, "E3.0.6.3", {"start": v(0, 8.88) * mm, "end": v(1.27, 8.88) * mm});
            skLineSegment(sketch, "E3.0.7.0", {"start": v(1.27, 8.9) * mm, "end": v(1.27, 10.15) * mm});
            skLineSegment(sketch, "E3.0.7.1", {"start": v(0, 8.9) * mm, "end": v(0, 10.15) * mm});
            skLineSegment(sketch, "E3.0.7.2", {"start": v(0, 8.9) * mm, "end": v(1.27, 8.9) * mm});
            skLineSegment(sketch, "E3.0.7.3", {"start": v(0, 10.15) * mm, "end": v(1.27, 10.15) * mm});
            skLineSegment(sketch, "E3.0.8.0", {"start": v(1.27, 10.16) * mm, "end": v(1.27, 11.42) * mm});
            skLineSegment(sketch, "E3.0.8.1", {"start": v(0, 10.16) * mm, "end": v(0, 11.42) * mm});
            skLineSegment(sketch, "E3.0.8.2", {"start": v(0, 10.16) * mm, "end": v(1.27, 10.16) * mm});
            skLineSegment(sketch, "E3.0.8.3", {"start": v(0, 11.42) * mm, "end": v(1.27, 11.42) * mm});
            skLineSegment(sketch, "E3.0.9.0", {"start": v(1.27, 11.43) * mm, "end": v(1.27, 12.7) * mm});
            skLineSegment(sketch, "E3.0.9.1", {"start": v(0, 11.43) * mm, "end": v(0, 12.7) * mm});
            skLineSegment(sketch, "E3.0.9.2", {"start": v(0, 11.43) * mm, "end": v(1.27, 11.43) * mm});
            skLineSegment(sketch, "E3.0.9.3", {"start": v(0, 12.7) * mm, "end": v(1.27, 12.7) * mm});
            skLineSegment(sketch, "E3.1.0.0", {"start": v(2.54, 0) * mm, "end": v(2.54, 1.26) * mm});
            skLineSegment(sketch, "E3.1.0.2", {"start": v(1.27, 0) * mm, "end": v(2.54, 0) * mm});
            skLineSegment(sketch, "E3.1.0.3", {"start": v(1.27, 1.26) * mm, "end": v(2.54, 1.26) * mm});
            skLineSegment(sketch, "E3.1.1.0", {"start": v(2.54, 1.27) * mm, "end": v(2.54, 2.53) * mm});
            skLineSegment(sketch, "E3.1.1.1", {"start": v(1.27, 1.27) * mm, "end": v(1.27, 2.53) * mm});
            skLineSegment(sketch, "E3.1.1.2", {"start": v(1.27, 1.27) * mm, "end": v(2.54, 1.27) * mm});
            skLineSegment(sketch, "E3.1.1.3", {"start": v(1.27, 2.53) * mm, "end": v(2.54, 2.53) * mm});
            skLineSegment(sketch, "E3.1.2.0", {"start": v(2.54, 2.54) * mm, "end": v(2.54, 3.8) * mm});
            skLineSegment(sketch, "E3.1.2.1", {"start": v(1.27, 2.54) * mm, "end": v(1.27, 3.8) * mm});
            skLineSegment(sketch, "E3.1.2.2", {"start": v(1.27, 2.54) * mm, "end": v(2.54, 2.54) * mm});
            skLineSegment(sketch, "E3.1.2.3", {"start": v(1.27, 3.8) * mm, "end": v(2.54, 3.8) * mm});
            skLineSegment(sketch, "E3.1.3.0", {"start": v(2.54, 3.81) * mm, "end": v(2.54, 5.07) * mm});
            skLineSegment(sketch, "E3.1.3.1", {"start": v(1.27, 3.81) * mm, "end": v(1.27, 5.07) * mm});
            skLineSegment(sketch, "E3.1.3.2", {"start": v(1.27, 3.81) * mm, "end": v(2.54, 3.81) * mm});
            skLineSegment(sketch, "E3.1.3.3", {"start": v(1.27, 5.07) * mm, "end": v(2.54, 5.07) * mm});
            skLineSegment(sketch, "E3.1.4.0", {"start": v(2.54, 5.08) * mm, "end": v(2.54, 6.34) * mm});
            skLineSegment(sketch, "E3.1.4.1", {"start": v(1.27, 5.08) * mm, "end": v(1.27, 6.34) * mm});
            skLineSegment(sketch, "E3.1.4.2", {"start": v(1.27, 5.08) * mm, "end": v(2.54, 5.08) * mm});
            skLineSegment(sketch, "E3.1.4.3", {"start": v(1.27, 6.34) * mm, "end": v(2.54, 6.34) * mm});
            skLineSegment(sketch, "E3.1.5.0", {"start": v(2.54, 6.35) * mm, "end": v(2.54, 7.61) * mm});
            skLineSegment(sketch, "E3.1.5.1", {"start": v(1.27, 6.35) * mm, "end": v(1.27, 7.61) * mm});
            skLineSegment(sketch, "E3.1.5.2", {"start": v(1.27, 6.35) * mm, "end": v(2.54, 6.35) * mm});
            skLineSegment(sketch, "E3.1.5.3", {"start": v(1.27, 7.61) * mm, "end": v(2.54, 7.61) * mm});
            skLineSegment(sketch, "E3.1.6.0", {"start": v(2.54, 7.62) * mm, "end": v(2.54, 8.88) * mm});
            skLineSegment(sketch, "E3.1.6.1", {"start": v(1.27, 7.62) * mm, "end": v(1.27, 8.88) * mm});
            skLineSegment(sketch, "E3.1.6.2", {"start": v(1.27, 7.62) * mm, "end": v(2.54, 7.62) * mm});
            skLineSegment(sketch, "E3.1.6.3", {"start": v(1.27, 8.88) * mm, "end": v(2.54, 8.88) * mm});
            skLineSegment(sketch, "E3.1.7.0", {"start": v(2.54, 8.9) * mm, "end": v(2.54, 10.15) * mm});
            skLineSegment(sketch, "E3.1.7.1", {"start": v(1.27, 8.9) * mm, "end": v(1.27, 10.15) * mm});
            skLineSegment(sketch, "E3.1.7.2", {"start": v(1.27, 8.9) * mm, "end": v(2.54, 8.9) * mm});
            skLineSegment(sketch, "E3.1.7.3", {"start": v(1.27, 10.15) * mm, "end": v(2.54, 10.15) * mm});
            skLineSegment(sketch, "E3.1.8.0", {"start": v(2.54, 10.16) * mm, "end": v(2.54, 11.42) * mm});
            skLineSegment(sketch, "E3.1.8.1", {"start": v(1.27, 10.16) * mm, "end": v(1.27, 11.42) * mm});
            skLineSegment(sketch, "E3.1.8.2", {"start": v(1.27, 10.16) * mm, "end": v(2.54, 10.16) * mm});
            skLineSegment(sketch, "E3.1.8.3", {"start": v(1.27, 11.42) * mm, "end": v(2.54, 11.42) * mm});
            skLineSegment(sketch, "E3.1.9.0", {"start": v(2.54, 11.43) * mm, "end": v(2.54, 12.7) * mm});
            skLineSegment(sketch, "E3.1.9.1", {"start": v(1.27, 11.43) * mm, "end": v(1.27, 12.7) * mm});
            skLineSegment(sketch, "E3.1.9.2", {"start": v(1.27, 11.43) * mm, "end": v(2.54, 11.43) * mm});
            skLineSegment(sketch, "E3.1.9.3", {"start": v(1.27, 12.7) * mm, "end": v(2.54, 12.7) * mm});
            skLineSegment(sketch, "E3.2.0.0", {"start": v(3.8, 0) * mm, "end": v(3.8, 1.26) * mm});
            skLineSegment(sketch, "E3.2.0.1", {"start": v(2.54, 0) * mm, "end": v(2.54, 1.26) * mm});
            skLineSegment(sketch, "E3.2.0.2", {"start": v(2.54, 0) * mm, "end": v(3.8, 0) * mm});
            skLineSegment(sketch, "E3.2.0.3", {"start": v(2.54, 1.26) * mm, "end": v(3.8, 1.26) * mm});
            skLineSegment(sketch, "E3.2.1.0", {"start": v(3.8, 1.27) * mm, "end": v(3.8, 2.53) * mm});
            skLineSegment(sketch, "E3.2.1.1", {"start": v(2.54, 1.27) * mm, "end": v(2.54, 2.53) * mm});
            skLineSegment(sketch, "E3.2.1.2", {"start": v(2.54, 1.27) * mm, "end": v(3.8, 1.27) * mm});
            skLineSegment(sketch, "E3.2.1.3", {"start": v(2.54, 2.53) * mm, "end": v(3.8, 2.53) * mm});
            skLineSegment(sketch, "E3.2.2.0", {"start": v(3.8, 2.54) * mm, "end": v(3.8, 3.8) * mm});
            skLineSegment(sketch, "E3.2.2.1", {"start": v(2.54, 2.54) * mm, "end": v(2.54, 3.8) * mm});
            skLineSegment(sketch, "E3.2.2.2", {"start": v(2.54, 2.54) * mm, "end": v(3.8, 2.54) * mm});
            skLineSegment(sketch, "E3.2.2.3", {"start": v(2.54, 3.8) * mm, "end": v(3.8, 3.8) * mm});
            skLineSegment(sketch, "E3.2.3.0", {"start": v(3.8, 3.81) * mm, "end": v(3.8, 5.07) * mm});
            skLineSegment(sketch, "E3.2.3.1", {"start": v(2.54, 3.81) * mm, "end": v(2.54, 5.07) * mm});
            skLineSegment(sketch, "E3.2.3.2", {"start": v(2.54, 3.81) * mm, "end": v(3.8, 3.81) * mm});
            skLineSegment(sketch, "E3.2.3.3", {"start": v(2.54, 5.07) * mm, "end": v(3.8, 5.07) * mm});
            skLineSegment(sketch, "E3.2.4.0", {"start": v(3.8, 5.08) * mm, "end": v(3.8, 6.34) * mm});
            skLineSegment(sketch, "E3.2.4.1", {"start": v(2.54, 5.08) * mm, "end": v(2.54, 6.34) * mm});
            skLineSegment(sketch, "E3.2.4.2", {"start": v(2.54, 5.08) * mm, "end": v(3.8, 5.08) * mm});
            skLineSegment(sketch, "E3.2.4.3", {"start": v(2.54, 6.34) * mm, "end": v(3.8, 6.34) * mm});
            skLineSegment(sketch, "E3.2.5.0", {"start": v(3.8, 6.35) * mm, "end": v(3.8, 7.61) * mm});
            skLineSegment(sketch, "E3.2.5.1", {"start": v(2.54, 6.35) * mm, "end": v(2.54, 7.61) * mm});
            skLineSegment(sketch, "E3.2.5.2", {"start": v(2.54, 6.35) * mm, "end": v(3.8, 6.35) * mm});
            skLineSegment(sketch, "E3.2.5.3", {"start": v(2.54, 7.61) * mm, "end": v(3.8, 7.61) * mm});
            skLineSegment(sketch, "E3.2.6.0", {"start": v(3.8, 7.62) * mm, "end": v(3.8, 8.88) * mm});
            skLineSegment(sketch, "E3.2.6.1", {"start": v(2.54, 7.62) * mm, "end": v(2.54, 8.88) * mm});
            skLineSegment(sketch, "E3.2.6.2", {"start": v(2.54, 7.62) * mm, "end": v(3.8, 7.62) * mm});
            skLineSegment(sketch, "E3.2.6.3", {"start": v(2.54, 8.88) * mm, "end": v(3.8, 8.88) * mm});
            skLineSegment(sketch, "E3.2.7.0", {"start": v(3.8, 8.9) * mm, "end": v(3.8, 10.15) * mm});
            skLineSegment(sketch, "E3.2.7.1", {"start": v(2.54, 8.9) * mm, "end": v(2.54, 10.15) * mm});
            skLineSegment(sketch, "E3.2.7.2", {"start": v(2.54, 8.9) * mm, "end": v(3.8, 8.9) * mm});
            skLineSegment(sketch, "E3.2.7.3", {"start": v(2.54, 10.15) * mm, "end": v(3.8, 10.15) * mm});
            skLineSegment(sketch, "E3.2.8.0", {"start": v(3.8, 10.16) * mm, "end": v(3.8, 11.42) * mm});
            skLineSegment(sketch, "E3.2.8.1", {"start": v(2.54, 10.16) * mm, "end": v(2.54, 11.42) * mm});
            skLineSegment(sketch, "E3.2.8.2", {"start": v(2.54, 10.16) * mm, "end": v(3.8, 10.16) * mm});
            skLineSegment(sketch, "E3.2.8.3", {"start": v(2.54, 11.42) * mm, "end": v(3.8, 11.42) * mm});
            skLineSegment(sketch, "E3.2.9.0", {"start": v(3.8, 11.43) * mm, "end": v(3.8, 12.7) * mm});
            skLineSegment(sketch, "E3.2.9.1", {"start": v(2.54, 11.43) * mm, "end": v(2.54, 12.7) * mm});
            skLineSegment(sketch, "E3.2.9.2", {"start": v(2.54, 11.43) * mm, "end": v(3.8, 11.43) * mm});
            skLineSegment(sketch, "E3.2.9.3", {"start": v(2.54, 12.7) * mm, "end": v(3.8, 12.7) * mm});
            skLineSegment(sketch, "E3.3.0.0", {"start": v(5.08, 0) * mm, "end": v(5.08, 1.26) * mm});
            skLineSegment(sketch, "E3.3.0.1", {"start": v(3.81, 0) * mm, "end": v(3.81, 1.26) * mm});
            skLineSegment(sketch, "E3.3.0.2", {"start": v(3.81, 0) * mm, "end": v(5.08, 0) * mm});
            skLineSegment(sketch, "E3.3.0.3", {"start": v(3.81, 1.26) * mm, "end": v(5.08, 1.26) * mm});
            skLineSegment(sketch, "E3.3.1.0", {"start": v(5.08, 1.27) * mm, "end": v(5.08, 2.53) * mm});
            skLineSegment(sketch, "E3.3.1.1", {"start": v(3.81, 1.27) * mm, "end": v(3.81, 2.53) * mm});
            skLineSegment(sketch, "E3.3.1.2", {"start": v(3.81, 1.27) * mm, "end": v(5.08, 1.27) * mm});
            skLineSegment(sketch, "E3.3.1.3", {"start": v(3.81, 2.53) * mm, "end": v(5.08, 2.53) * mm});
            skLineSegment(sketch, "E3.3.2.0", {"start": v(5.08, 2.54) * mm, "end": v(5.08, 3.8) * mm});
            skLineSegment(sketch, "E3.3.2.1", {"start": v(3.81, 2.54) * mm, "end": v(3.81, 3.8) * mm});
            skLineSegment(sketch, "E3.3.2.2", {"start": v(3.81, 2.54) * mm, "end": v(5.08, 2.54) * mm});
            skLineSegment(sketch, "E3.3.2.3", {"start": v(3.81, 3.8) * mm, "end": v(5.08, 3.8) * mm});
            skLineSegment(sketch, "E3.3.3.0", {"start": v(5.08, 3.81) * mm, "end": v(5.08, 5.07) * mm});
            skLineSegment(sketch, "E3.3.3.1", {"start": v(3.81, 3.81) * mm, "end": v(3.81, 5.07) * mm});
            skLineSegment(sketch, "E3.3.3.2", {"start": v(3.81, 3.81) * mm, "end": v(5.08, 3.81) * mm});
            skLineSegment(sketch, "E3.3.3.3", {"start": v(3.81, 5.07) * mm, "end": v(5.08, 5.07) * mm});
            skLineSegment(sketch, "E3.3.4.0", {"start": v(5.08, 5.08) * mm, "end": v(5.08, 6.34) * mm});
            skLineSegment(sketch, "E3.3.4.1", {"start": v(3.81, 5.08) * mm, "end": v(3.81, 6.34) * mm});
            skLineSegment(sketch, "E3.3.4.2", {"start": v(3.81, 5.08) * mm, "end": v(5.08, 5.08) * mm});
            skLineSegment(sketch, "E3.3.4.3", {"start": v(3.81, 6.34) * mm, "end": v(5.08, 6.34) * mm});
            skLineSegment(sketch, "E3.3.5.0", {"start": v(5.08, 6.35) * mm, "end": v(5.08, 7.61) * mm});
            skLineSegment(sketch, "E3.3.5.1", {"start": v(3.81, 6.35) * mm, "end": v(3.81, 7.61) * mm});
            skLineSegment(sketch, "E3.3.5.2", {"start": v(3.81, 6.35) * mm, "end": v(5.08, 6.35) * mm});
            skLineSegment(sketch, "E3.3.5.3", {"start": v(3.81, 7.61) * mm, "end": v(5.08, 7.61) * mm});
            skLineSegment(sketch, "E3.3.6.0", {"start": v(5.08, 7.62) * mm, "end": v(5.08, 8.88) * mm});
            skLineSegment(sketch, "E3.3.6.1", {"start": v(3.81, 7.62) * mm, "end": v(3.81, 8.88) * mm});
            skLineSegment(sketch, "E3.3.6.2", {"start": v(3.81, 7.62) * mm, "end": v(5.08, 7.62) * mm});
            skLineSegment(sketch, "E3.3.6.3", {"start": v(3.81, 8.88) * mm, "end": v(5.08, 8.88) * mm});
            skLineSegment(sketch, "E3.3.7.0", {"start": v(5.08, 8.9) * mm, "end": v(5.08, 10.15) * mm});
            skLineSegment(sketch, "E3.3.7.1", {"start": v(3.81, 8.9) * mm, "end": v(3.81, 10.15) * mm});
            skLineSegment(sketch, "E3.3.7.2", {"start": v(3.81, 8.9) * mm, "end": v(5.08, 8.9) * mm});
            skLineSegment(sketch, "E3.3.7.3", {"start": v(3.81, 10.15) * mm, "end": v(5.08, 10.15) * mm});
            skLineSegment(sketch, "E3.3.8.0", {"start": v(5.08, 10.16) * mm, "end": v(5.08, 11.42) * mm});
            skLineSegment(sketch, "E3.3.8.1", {"start": v(3.81, 10.16) * mm, "end": v(3.81, 11.42) * mm});
            skLineSegment(sketch, "E3.3.8.2", {"start": v(3.81, 10.16) * mm, "end": v(5.08, 10.16) * mm});
            skLineSegment(sketch, "E3.3.8.3", {"start": v(3.81, 11.42) * mm, "end": v(5.08, 11.42) * mm});
            skLineSegment(sketch, "E3.3.9.0", {"start": v(5.08, 11.43) * mm, "end": v(5.08, 12.7) * mm});
            skLineSegment(sketch, "E3.3.9.1", {"start": v(3.81, 11.43) * mm, "end": v(3.81, 12.7) * mm});
            skLineSegment(sketch, "E3.3.9.2", {"start": v(3.81, 11.43) * mm, "end": v(5.08, 11.43) * mm});
            skLineSegment(sketch, "E3.3.9.3", {"start": v(3.81, 12.7) * mm, "end": v(5.08, 12.7) * mm});
            skLineSegment(sketch, "E3.4.0.0", {"start": v(6.35, 0) * mm, "end": v(6.35, 1.26) * mm});
            skLineSegment(sketch, "E3.4.0.1", {"start": v(5.08, 0) * mm, "end": v(5.08, 1.26) * mm});
            skLineSegment(sketch, "E3.4.0.2", {"start": v(5.08, 0) * mm, "end": v(6.35, 0) * mm});
            skLineSegment(sketch, "E3.4.0.3", {"start": v(5.08, 1.26) * mm, "end": v(6.35, 1.26) * mm});
            skLineSegment(sketch, "E3.4.1.0", {"start": v(6.35, 1.27) * mm, "end": v(6.35, 2.53) * mm});
            skLineSegment(sketch, "E3.4.1.1", {"start": v(5.08, 1.27) * mm, "end": v(5.08, 2.53) * mm});
            skLineSegment(sketch, "E3.4.1.2", {"start": v(5.08, 1.27) * mm, "end": v(6.35, 1.27) * mm});
            skLineSegment(sketch, "E3.4.1.3", {"start": v(5.08, 2.53) * mm, "end": v(6.35, 2.53) * mm});
            skLineSegment(sketch, "E3.4.2.0", {"start": v(6.35, 2.54) * mm, "end": v(6.35, 3.8) * mm});
            skLineSegment(sketch, "E3.4.2.1", {"start": v(5.08, 2.54) * mm, "end": v(5.08, 3.8) * mm});
            skLineSegment(sketch, "E3.4.2.2", {"start": v(5.08, 2.54) * mm, "end": v(6.35, 2.54) * mm});
            skLineSegment(sketch, "E3.4.2.3", {"start": v(5.08, 3.8) * mm, "end": v(6.35, 3.8) * mm});
            skLineSegment(sketch, "E3.4.3.0", {"start": v(6.35, 3.81) * mm, "end": v(6.35, 5.07) * mm});
            skLineSegment(sketch, "E3.4.3.1", {"start": v(5.08, 3.81) * mm, "end": v(5.08, 5.07) * mm});
            skLineSegment(sketch, "E3.4.3.2", {"start": v(5.08, 3.81) * mm, "end": v(6.35, 3.81) * mm});
            skLineSegment(sketch, "E3.4.3.3", {"start": v(5.08, 5.07) * mm, "end": v(6.35, 5.07) * mm});
            skLineSegment(sketch, "E3.4.4.0", {"start": v(6.35, 5.08) * mm, "end": v(6.35, 6.34) * mm});
            skLineSegment(sketch, "E3.4.4.1", {"start": v(5.08, 5.08) * mm, "end": v(5.08, 6.34) * mm});
            skLineSegment(sketch, "E3.4.4.2", {"start": v(5.08, 5.08) * mm, "end": v(6.35, 5.08) * mm});
            skLineSegment(sketch, "E3.4.4.3", {"start": v(5.08, 6.34) * mm, "end": v(6.35, 6.34) * mm});
            skLineSegment(sketch, "E3.4.5.0", {"start": v(6.35, 6.35) * mm, "end": v(6.35, 7.61) * mm});
            skLineSegment(sketch, "E3.4.5.1", {"start": v(5.08, 6.35) * mm, "end": v(5.08, 7.61) * mm});
            skLineSegment(sketch, "E3.4.5.2", {"start": v(5.08, 6.35) * mm, "end": v(6.35, 6.35) * mm});
            skLineSegment(sketch, "E3.4.5.3", {"start": v(5.08, 7.61) * mm, "end": v(6.35, 7.61) * mm});
            skLineSegment(sketch, "E3.4.6.0", {"start": v(6.35, 7.62) * mm, "end": v(6.35, 8.88) * mm});
            skLineSegment(sketch, "E3.4.6.1", {"start": v(5.08, 7.62) * mm, "end": v(5.08, 8.88) * mm});
            skLineSegment(sketch, "E3.4.6.2", {"start": v(5.08, 7.62) * mm, "end": v(6.35, 7.62) * mm});
            skLineSegment(sketch, "E3.4.6.3", {"start": v(5.08, 8.88) * mm, "end": v(6.35, 8.88) * mm});
            skLineSegment(sketch, "E3.4.7.0", {"start": v(6.35, 8.9) * mm, "end": v(6.35, 10.15) * mm});
            skLineSegment(sketch, "E3.4.7.1", {"start": v(5.08, 8.9) * mm, "end": v(5.08, 10.15) * mm});
            skLineSegment(sketch, "E3.4.7.2", {"start": v(5.08, 8.9) * mm, "end": v(6.35, 8.9) * mm});
            skLineSegment(sketch, "E3.4.7.3", {"start": v(5.08, 10.15) * mm, "end": v(6.35, 10.15) * mm});
            skLineSegment(sketch, "E3.4.8.0", {"start": v(6.35, 10.16) * mm, "end": v(6.35, 11.42) * mm});
            skLineSegment(sketch, "E3.4.8.1", {"start": v(5.08, 10.16) * mm, "end": v(5.08, 11.42) * mm});
            skLineSegment(sketch, "E3.4.8.2", {"start": v(5.08, 10.16) * mm, "end": v(6.35, 10.16) * mm});
            skLineSegment(sketch, "E3.4.8.3", {"start": v(5.08, 11.42) * mm, "end": v(6.35, 11.42) * mm});
            skLineSegment(sketch, "E3.4.9.0", {"start": v(6.35, 11.43) * mm, "end": v(6.35, 12.7) * mm});
            skLineSegment(sketch, "E3.4.9.1", {"start": v(5.08, 11.43) * mm, "end": v(5.08, 12.7) * mm});
            skLineSegment(sketch, "E3.4.9.2", {"start": v(5.08, 11.43) * mm, "end": v(6.35, 11.43) * mm});
            skLineSegment(sketch, "E3.4.9.3", {"start": v(5.08, 12.7) * mm, "end": v(6.35, 12.7) * mm});
            skLineSegment(sketch, "E3.5.0.0", {"start": v(7.62, 0) * mm, "end": v(7.62, 1.26) * mm});
            skLineSegment(sketch, "E3.5.0.1", {"start": v(6.35, 0) * mm, "end": v(6.35, 1.26) * mm});
            skLineSegment(sketch, "E3.5.0.2", {"start": v(6.35, 0) * mm, "end": v(7.62, 0) * mm});
            skLineSegment(sketch, "E3.5.0.3", {"start": v(6.35, 1.26) * mm, "end": v(7.62, 1.26) * mm});
            skLineSegment(sketch, "E3.5.1.0", {"start": v(7.62, 1.27) * mm, "end": v(7.62, 2.53) * mm});
            skLineSegment(sketch, "E3.5.1.1", {"start": v(6.35, 1.27) * mm, "end": v(6.35, 2.53) * mm});
            skLineSegment(sketch, "E3.5.1.2", {"start": v(6.35, 1.27) * mm, "end": v(7.62, 1.27) * mm});
            skLineSegment(sketch, "E3.5.1.3", {"start": v(6.35, 2.53) * mm, "end": v(7.62, 2.53) * mm});
            skLineSegment(sketch, "E3.5.2.0", {"start": v(7.62, 2.54) * mm, "end": v(7.62, 3.8) * mm});
            skLineSegment(sketch, "E3.5.2.1", {"start": v(6.35, 2.54) * mm, "end": v(6.35, 3.8) * mm});
            skLineSegment(sketch, "E3.5.2.2", {"start": v(6.35, 2.54) * mm, "end": v(7.62, 2.54) * mm});
            skLineSegment(sketch, "E3.5.2.3", {"start": v(6.35, 3.8) * mm, "end": v(7.62, 3.8) * mm});
            skLineSegment(sketch, "E3.5.3.0", {"start": v(7.62, 3.81) * mm, "end": v(7.62, 5.07) * mm});
            skLineSegment(sketch, "E3.5.3.1", {"start": v(6.35, 3.81) * mm, "end": v(6.35, 5.07) * mm});
            skLineSegment(sketch, "E3.5.3.2", {"start": v(6.35, 3.81) * mm, "end": v(7.62, 3.81) * mm});
            skLineSegment(sketch, "E3.5.3.3", {"start": v(6.35, 5.07) * mm, "end": v(7.62, 5.07) * mm});
            skLineSegment(sketch, "E3.5.4.0", {"start": v(7.62, 5.08) * mm, "end": v(7.62, 6.34) * mm});
            skLineSegment(sketch, "E3.5.4.1", {"start": v(6.35, 5.08) * mm, "end": v(6.35, 6.34) * mm});
            skLineSegment(sketch, "E3.5.4.2", {"start": v(6.35, 5.08) * mm, "end": v(7.62, 5.08) * mm});
            skLineSegment(sketch, "E3.5.4.3", {"start": v(6.35, 6.34) * mm, "end": v(7.62, 6.34) * mm});
            skLineSegment(sketch, "E3.5.5.0", {"start": v(7.62, 6.35) * mm, "end": v(7.62, 7.61) * mm});
            skLineSegment(sketch, "E3.5.5.1", {"start": v(6.35, 6.35) * mm, "end": v(6.35, 7.61) * mm});
            skLineSegment(sketch, "E3.5.5.2", {"start": v(6.35, 6.35) * mm, "end": v(7.62, 6.35) * mm});
            skLineSegment(sketch, "E3.5.5.3", {"start": v(6.35, 7.61) * mm, "end": v(7.62, 7.61) * mm});
            skLineSegment(sketch, "E3.5.6.0", {"start": v(7.62, 7.62) * mm, "end": v(7.62, 8.88) * mm});
            skLineSegment(sketch, "E3.5.6.1", {"start": v(6.35, 7.62) * mm, "end": v(6.35, 8.88) * mm});
            skLineSegment(sketch, "E3.5.6.2", {"start": v(6.35, 7.62) * mm, "end": v(7.62, 7.62) * mm});
            skLineSegment(sketch, "E3.5.6.3", {"start": v(6.35, 8.88) * mm, "end": v(7.62, 8.88) * mm});
            skLineSegment(sketch, "E3.5.7.0", {"start": v(7.62, 8.9) * mm, "end": v(7.62, 10.15) * mm});
            skLineSegment(sketch, "E3.5.7.1", {"start": v(6.35, 8.9) * mm, "end": v(6.35, 10.15) * mm});
            skLineSegment(sketch, "E3.5.7.2", {"start": v(6.35, 8.9) * mm, "end": v(7.62, 8.9) * mm});
            skLineSegment(sketch, "E3.5.7.3", {"start": v(6.35, 10.15) * mm, "end": v(7.62, 10.15) * mm});
            skLineSegment(sketch, "E3.5.8.0", {"start": v(7.62, 10.16) * mm, "end": v(7.62, 11.42) * mm});
            skLineSegment(sketch, "E3.5.8.1", {"start": v(6.35, 10.16) * mm, "end": v(6.35, 11.42) * mm});
            skLineSegment(sketch, "E3.5.8.2", {"start": v(6.35, 10.16) * mm, "end": v(7.62, 10.16) * mm});
            skLineSegment(sketch, "E3.5.8.3", {"start": v(6.35, 11.42) * mm, "end": v(7.62, 11.42) * mm});
            skLineSegment(sketch, "E3.5.9.0", {"start": v(7.62, 11.43) * mm, "end": v(7.62, 12.7) * mm});
            skLineSegment(sketch, "E3.5.9.1", {"start": v(6.35, 11.43) * mm, "end": v(6.35, 12.7) * mm});
            skLineSegment(sketch, "E3.5.9.2", {"start": v(6.35, 11.43) * mm, "end": v(7.62, 11.43) * mm});
            skLineSegment(sketch, "E3.5.9.3", {"start": v(6.35, 12.7) * mm, "end": v(7.62, 12.7) * mm});
            skLineSegment(sketch, "E3.6.0.0", {"start": v(8.89, 0) * mm, "end": v(8.89, 1.26) * mm});
            skLineSegment(sketch, "E3.6.0.1", {"start": v(7.62, 0) * mm, "end": v(7.62, 1.26) * mm});
            skLineSegment(sketch, "E3.6.0.2", {"start": v(7.62, 0) * mm, "end": v(8.89, 0) * mm});
            skLineSegment(sketch, "E3.6.0.3", {"start": v(7.62, 1.26) * mm, "end": v(8.89, 1.26) * mm});
            skLineSegment(sketch, "E3.6.1.0", {"start": v(8.89, 1.27) * mm, "end": v(8.89, 2.53) * mm});
            skLineSegment(sketch, "E3.6.1.1", {"start": v(7.62, 1.27) * mm, "end": v(7.62, 2.53) * mm});
            skLineSegment(sketch, "E3.6.1.2", {"start": v(7.62, 1.27) * mm, "end": v(8.89, 1.27) * mm});
            skLineSegment(sketch, "E3.6.1.3", {"start": v(7.62, 2.53) * mm, "end": v(8.89, 2.53) * mm});
            skLineSegment(sketch, "E3.6.2.0", {"start": v(8.89, 2.54) * mm, "end": v(8.89, 3.8) * mm});
            skLineSegment(sketch, "E3.6.2.1", {"start": v(7.62, 2.54) * mm, "end": v(7.62, 3.8) * mm});
            skLineSegment(sketch, "E3.6.2.2", {"start": v(7.62, 2.54) * mm, "end": v(8.89, 2.54) * mm});
            skLineSegment(sketch, "E3.6.2.3", {"start": v(7.62, 3.8) * mm, "end": v(8.89, 3.8) * mm});
            skLineSegment(sketch, "E3.6.3.0", {"start": v(8.89, 3.81) * mm, "end": v(8.89, 5.07) * mm});
            skLineSegment(sketch, "E3.6.3.1", {"start": v(7.62, 3.81) * mm, "end": v(7.62, 5.07) * mm});
            skLineSegment(sketch, "E3.6.3.2", {"start": v(7.62, 3.81) * mm, "end": v(8.89, 3.81) * mm});
            skLineSegment(sketch, "E3.6.3.3", {"start": v(7.62, 5.07) * mm, "end": v(8.89, 5.07) * mm});
            skLineSegment(sketch, "E3.6.4.0", {"start": v(8.89, 5.08) * mm, "end": v(8.89, 6.34) * mm});
            skLineSegment(sketch, "E3.6.4.1", {"start": v(7.62, 5.08) * mm, "end": v(7.62, 6.34) * mm});
            skLineSegment(sketch, "E3.6.4.2", {"start": v(7.62, 5.08) * mm, "end": v(8.89, 5.08) * mm});
            skLineSegment(sketch, "E3.6.4.3", {"start": v(7.62, 6.34) * mm, "end": v(8.89, 6.34) * mm});
            skLineSegment(sketch, "E3.6.5.0", {"start": v(8.89, 6.35) * mm, "end": v(8.89, 7.61) * mm});
            skLineSegment(sketch, "E3.6.5.1", {"start": v(7.62, 6.35) * mm, "end": v(7.62, 7.61) * mm});
            skLineSegment(sketch, "E3.6.5.2", {"start": v(7.62, 6.35) * mm, "end": v(8.89, 6.35) * mm});
            skLineSegment(sketch, "E3.6.5.3", {"start": v(7.62, 7.61) * mm, "end": v(8.89, 7.61) * mm});
            skLineSegment(sketch, "E3.6.6.0", {"start": v(8.89, 7.62) * mm, "end": v(8.89, 8.88) * mm});
            skLineSegment(sketch, "E3.6.6.1", {"start": v(7.62, 7.62) * mm, "end": v(7.62, 8.88) * mm});
            skLineSegment(sketch, "E3.6.6.2", {"start": v(7.62, 7.62) * mm, "end": v(8.89, 7.62) * mm});
            skLineSegment(sketch, "E3.6.6.3", {"start": v(7.62, 8.88) * mm, "end": v(8.89, 8.88) * mm});
            skLineSegment(sketch, "E3.6.7.0", {"start": v(8.89, 8.9) * mm, "end": v(8.89, 10.15) * mm});
            skLineSegment(sketch, "E3.6.7.1", {"start": v(7.62, 8.9) * mm, "end": v(7.62, 10.15) * mm});
            skLineSegment(sketch, "E3.6.7.2", {"start": v(7.62, 8.9) * mm, "end": v(8.89, 8.9) * mm});
            skLineSegment(sketch, "E3.6.7.3", {"start": v(7.62, 10.15) * mm, "end": v(8.89, 10.15) * mm});
            skLineSegment(sketch, "E3.6.8.0", {"start": v(8.89, 10.16) * mm, "end": v(8.89, 11.42) * mm});
            skLineSegment(sketch, "E3.6.8.1", {"start": v(7.62, 10.16) * mm, "end": v(7.62, 11.42) * mm});
            skLineSegment(sketch, "E3.6.8.2", {"start": v(7.62, 10.16) * mm, "end": v(8.89, 10.16) * mm});
            skLineSegment(sketch, "E3.6.8.3", {"start": v(7.62, 11.42) * mm, "end": v(8.89, 11.42) * mm});
            skLineSegment(sketch, "E3.6.9.0", {"start": v(8.89, 11.43) * mm, "end": v(8.89, 12.7) * mm});
            skLineSegment(sketch, "E3.6.9.1", {"start": v(7.62, 11.43) * mm, "end": v(7.62, 12.7) * mm});
            skLineSegment(sketch, "E3.6.9.2", {"start": v(7.62, 11.43) * mm, "end": v(8.89, 11.43) * mm});
            skLineSegment(sketch, "E3.6.9.3", {"start": v(7.62, 12.7) * mm, "end": v(8.89, 12.7) * mm});
            skLineSegment(sketch, "E3.7.0.0", {"start": v(10.16, 0) * mm, "end": v(10.16, 1.26) * mm});
            skLineSegment(sketch, "E3.7.0.1", {"start": v(8.9, 0) * mm, "end": v(8.9, 1.26) * mm});
            skLineSegment(sketch, "E3.7.0.2", {"start": v(8.9, 0) * mm, "end": v(10.16, 0) * mm});
            skLineSegment(sketch, "E3.7.0.3", {"start": v(8.9, 1.26) * mm, "end": v(10.16, 1.26) * mm});
            skLineSegment(sketch, "E3.7.1.0", {"start": v(10.16, 1.27) * mm, "end": v(10.16, 2.53) * mm});
            skLineSegment(sketch, "E3.7.1.1", {"start": v(8.9, 1.27) * mm, "end": v(8.9, 2.53) * mm});
            skLineSegment(sketch, "E3.7.1.2", {"start": v(8.9, 1.27) * mm, "end": v(10.16, 1.27) * mm});
            skLineSegment(sketch, "E3.7.1.3", {"start": v(8.9, 2.53) * mm, "end": v(10.16, 2.53) * mm});
            skLineSegment(sketch, "E3.7.2.0", {"start": v(10.16, 2.54) * mm, "end": v(10.16, 3.8) * mm});
            skLineSegment(sketch, "E3.7.2.1", {"start": v(8.9, 2.54) * mm, "end": v(8.9, 3.8) * mm});
            skLineSegment(sketch, "E3.7.2.2", {"start": v(8.9, 2.54) * mm, "end": v(10.16, 2.54) * mm});
            skLineSegment(sketch, "E3.7.2.3", {"start": v(8.9, 3.8) * mm, "end": v(10.16, 3.8) * mm});
            skLineSegment(sketch, "E3.7.3.0", {"start": v(10.16, 3.81) * mm, "end": v(10.16, 5.07) * mm});
            skLineSegment(sketch, "E3.7.3.1", {"start": v(8.9, 3.81) * mm, "end": v(8.9, 5.07) * mm});
            skLineSegment(sketch, "E3.7.3.2", {"start": v(8.9, 3.81) * mm, "end": v(10.16, 3.81) * mm});
            skLineSegment(sketch, "E3.7.3.3", {"start": v(8.9, 5.07) * mm, "end": v(10.16, 5.07) * mm});
            skLineSegment(sketch, "E3.7.4.0", {"start": v(10.16, 5.08) * mm, "end": v(10.16, 6.34) * mm});
            skLineSegment(sketch, "E3.7.4.1", {"start": v(8.9, 5.08) * mm, "end": v(8.9, 6.34) * mm});
            skLineSegment(sketch, "E3.7.4.2", {"start": v(8.9, 5.08) * mm, "end": v(10.16, 5.08) * mm});
            skLineSegment(sketch, "E3.7.4.3", {"start": v(8.9, 6.34) * mm, "end": v(10.16, 6.34) * mm});
            skLineSegment(sketch, "E3.7.5.0", {"start": v(10.16, 6.35) * mm, "end": v(10.16, 7.61) * mm});
            skLineSegment(sketch, "E3.7.5.1", {"start": v(8.9, 6.35) * mm, "end": v(8.9, 7.61) * mm});
            skLineSegment(sketch, "E3.7.5.2", {"start": v(8.9, 6.35) * mm, "end": v(10.16, 6.35) * mm});
            skLineSegment(sketch, "E3.7.5.3", {"start": v(8.9, 7.61) * mm, "end": v(10.16, 7.61) * mm});
            skLineSegment(sketch, "E3.7.6.0", {"start": v(10.16, 7.62) * mm, "end": v(10.16, 8.88) * mm});
            skLineSegment(sketch, "E3.7.6.1", {"start": v(8.9, 7.62) * mm, "end": v(8.9, 8.88) * mm});
            skLineSegment(sketch, "E3.7.6.2", {"start": v(8.9, 7.62) * mm, "end": v(10.16, 7.62) * mm});
            skLineSegment(sketch, "E3.7.6.3", {"start": v(8.9, 8.88) * mm, "end": v(10.16, 8.88) * mm});
            skLineSegment(sketch, "E3.7.7.0", {"start": v(10.16, 8.9) * mm, "end": v(10.16, 10.15) * mm});
            skLineSegment(sketch, "E3.7.7.1", {"start": v(8.9, 8.9) * mm, "end": v(8.9, 10.15) * mm});
            skLineSegment(sketch, "E3.7.7.2", {"start": v(8.9, 8.9) * mm, "end": v(10.16, 8.9) * mm});
            skLineSegment(sketch, "E3.7.7.3", {"start": v(8.9, 10.15) * mm, "end": v(10.16, 10.15) * mm});
            skLineSegment(sketch, "E3.7.8.0", {"start": v(10.16, 10.16) * mm, "end": v(10.16, 11.42) * mm});
            skLineSegment(sketch, "E3.7.8.1", {"start": v(8.9, 10.16) * mm, "end": v(8.9, 11.42) * mm});
            skLineSegment(sketch, "E3.7.8.2", {"start": v(8.9, 10.16) * mm, "end": v(10.16, 10.16) * mm});
            skLineSegment(sketch, "E3.7.8.3", {"start": v(8.9, 11.42) * mm, "end": v(10.16, 11.42) * mm});
            skLineSegment(sketch, "E3.7.9.0", {"start": v(10.16, 11.43) * mm, "end": v(10.16, 12.7) * mm});
            skLineSegment(sketch, "E3.7.9.1", {"start": v(8.9, 11.43) * mm, "end": v(8.9, 12.7) * mm});
            skLineSegment(sketch, "E3.7.9.2", {"start": v(8.9, 11.43) * mm, "end": v(10.16, 11.43) * mm});
            skLineSegment(sketch, "E3.7.9.3", {"start": v(8.9, 12.7) * mm, "end": v(10.16, 12.7) * mm});
            skLineSegment(sketch, "E3.8.0.0", {"start": v(11.43, 0) * mm, "end": v(11.43, 1.26) * mm});
            skLineSegment(sketch, "E3.8.0.1", {"start": v(10.16, 0) * mm, "end": v(10.16, 1.26) * mm});
            skLineSegment(sketch, "E3.8.0.2", {"start": v(10.16, 0) * mm, "end": v(11.43, 0) * mm});
            skLineSegment(sketch, "E3.8.0.3", {"start": v(10.16, 1.26) * mm, "end": v(11.43, 1.26) * mm});
            skLineSegment(sketch, "E3.8.1.0", {"start": v(11.43, 1.27) * mm, "end": v(11.43, 2.53) * mm});
            skLineSegment(sketch, "E3.8.1.1", {"start": v(10.16, 1.27) * mm, "end": v(10.16, 2.53) * mm});
            skLineSegment(sketch, "E3.8.1.2", {"start": v(10.16, 1.27) * mm, "end": v(11.43, 1.27) * mm});
            skLineSegment(sketch, "E3.8.1.3", {"start": v(10.16, 2.53) * mm, "end": v(11.43, 2.53) * mm});
            skLineSegment(sketch, "E3.8.2.0", {"start": v(11.43, 2.54) * mm, "end": v(11.43, 3.8) * mm});
            skLineSegment(sketch, "E3.8.2.1", {"start": v(10.16, 2.54) * mm, "end": v(10.16, 3.8) * mm});
            skLineSegment(sketch, "E3.8.2.2", {"start": v(10.16, 2.54) * mm, "end": v(11.43, 2.54) * mm});
            skLineSegment(sketch, "E3.8.2.3", {"start": v(10.16, 3.8) * mm, "end": v(11.43, 3.8) * mm});
            skLineSegment(sketch, "E3.8.3.0", {"start": v(11.43, 3.81) * mm, "end": v(11.43, 5.07) * mm});
            skLineSegment(sketch, "E3.8.3.1", {"start": v(10.16, 3.81) * mm, "end": v(10.16, 5.07) * mm});
            skLineSegment(sketch, "E3.8.3.2", {"start": v(10.16, 3.81) * mm, "end": v(11.43, 3.81) * mm});
            skLineSegment(sketch, "E3.8.3.3", {"start": v(10.16, 5.07) * mm, "end": v(11.43, 5.07) * mm});
            skLineSegment(sketch, "E3.8.4.0", {"start": v(11.43, 5.08) * mm, "end": v(11.43, 6.34) * mm});
            skLineSegment(sketch, "E3.8.4.1", {"start": v(10.16, 5.08) * mm, "end": v(10.16, 6.34) * mm});
            skLineSegment(sketch, "E3.8.4.2", {"start": v(10.16, 5.08) * mm, "end": v(11.43, 5.08) * mm});
            skLineSegment(sketch, "E3.8.4.3", {"start": v(10.16, 6.34) * mm, "end": v(11.43, 6.34) * mm});
            skLineSegment(sketch, "E3.8.5.0", {"start": v(11.43, 6.35) * mm, "end": v(11.43, 7.61) * mm});
            skLineSegment(sketch, "E3.8.5.1", {"start": v(10.16, 6.35) * mm, "end": v(10.16, 7.61) * mm});
            skLineSegment(sketch, "E3.8.5.2", {"start": v(10.16, 6.35) * mm, "end": v(11.43, 6.35) * mm});
            skLineSegment(sketch, "E3.8.5.3", {"start": v(10.16, 7.61) * mm, "end": v(11.43, 7.61) * mm});
            skLineSegment(sketch, "E3.8.6.0", {"start": v(11.43, 7.62) * mm, "end": v(11.43, 8.88) * mm});
            skLineSegment(sketch, "E3.8.6.1", {"start": v(10.16, 7.62) * mm, "end": v(10.16, 8.88) * mm});
            skLineSegment(sketch, "E3.8.6.2", {"start": v(10.16, 7.62) * mm, "end": v(11.43, 7.62) * mm});
            skLineSegment(sketch, "E3.8.6.3", {"start": v(10.16, 8.88) * mm, "end": v(11.43, 8.88) * mm});
            skLineSegment(sketch, "E3.8.7.0", {"start": v(11.43, 8.9) * mm, "end": v(11.43, 10.15) * mm});
            skLineSegment(sketch, "E3.8.7.1", {"start": v(10.16, 8.9) * mm, "end": v(10.16, 10.15) * mm});
            skLineSegment(sketch, "E3.8.7.2", {"start": v(10.16, 8.9) * mm, "end": v(11.43, 8.9) * mm});
            skLineSegment(sketch, "E3.8.7.3", {"start": v(10.16, 10.15) * mm, "end": v(11.43, 10.15) * mm});
            skLineSegment(sketch, "E3.8.8.0", {"start": v(11.43, 10.16) * mm, "end": v(11.43, 11.42) * mm});
            skLineSegment(sketch, "E3.8.8.1", {"start": v(10.16, 10.16) * mm, "end": v(10.16, 11.42) * mm});
            skLineSegment(sketch, "E3.8.8.2", {"start": v(10.16, 10.16) * mm, "end": v(11.43, 10.16) * mm});
            skLineSegment(sketch, "E3.8.8.3", {"start": v(10.16, 11.42) * mm, "end": v(11.43, 11.42) * mm});
            skLineSegment(sketch, "E3.8.9.0", {"start": v(11.43, 11.43) * mm, "end": v(11.43, 12.7) * mm});
            skLineSegment(sketch, "E3.8.9.1", {"start": v(10.16, 11.43) * mm, "end": v(10.16, 12.7) * mm});
            skLineSegment(sketch, "E3.8.9.2", {"start": v(10.16, 11.43) * mm, "end": v(11.43, 11.43) * mm});
            skLineSegment(sketch, "E3.8.9.3", {"start": v(10.16, 12.7) * mm, "end": v(11.43, 12.7) * mm});
            skLineSegment(sketch, "E3.9.0.0", {"start": v(12.7, 0) * mm, "end": v(12.7, 1.26) * mm});
            skLineSegment(sketch, "E3.9.0.1", {"start": v(11.43, 0) * mm, "end": v(11.43, 1.26) * mm});
            skLineSegment(sketch, "E3.9.0.2", {"start": v(11.43, 0) * mm, "end": v(12.7, 0) * mm});
            skLineSegment(sketch, "E3.9.0.3", {"start": v(11.43, 1.26) * mm, "end": v(12.7, 1.26) * mm});
            skLineSegment(sketch, "E3.9.1.0", {"start": v(12.7, 1.27) * mm, "end": v(12.7, 2.53) * mm});
            skLineSegment(sketch, "E3.9.1.1", {"start": v(11.43, 1.27) * mm, "end": v(11.43, 2.53) * mm});
            skLineSegment(sketch, "E3.9.1.2", {"start": v(11.43, 1.27) * mm, "end": v(12.7, 1.27) * mm});
            skLineSegment(sketch, "E3.9.1.3", {"start": v(11.43, 2.53) * mm, "end": v(12.7, 2.53) * mm});
            skLineSegment(sketch, "E3.9.2.0", {"start": v(12.7, 2.54) * mm, "end": v(12.7, 3.8) * mm});
            skLineSegment(sketch, "E3.9.2.1", {"start": v(11.43, 2.54) * mm, "end": v(11.43, 3.8) * mm});
            skLineSegment(sketch, "E3.9.2.2", {"start": v(11.43, 2.54) * mm, "end": v(12.7, 2.54) * mm});
            skLineSegment(sketch, "E3.9.2.3", {"start": v(11.43, 3.8) * mm, "end": v(12.7, 3.8) * mm});
            skLineSegment(sketch, "E3.9.3.0", {"start": v(12.7, 3.81) * mm, "end": v(12.7, 5.07) * mm});
            skLineSegment(sketch, "E3.9.3.1", {"start": v(11.43, 3.81) * mm, "end": v(11.43, 5.07) * mm});
            skLineSegment(sketch, "E3.9.3.2", {"start": v(11.43, 3.81) * mm, "end": v(12.7, 3.81) * mm});
            skLineSegment(sketch, "E3.9.3.3", {"start": v(11.43, 5.07) * mm, "end": v(12.7, 5.07) * mm});
            skLineSegment(sketch, "E3.9.4.0", {"start": v(12.7, 5.08) * mm, "end": v(12.7, 6.34) * mm});
            skLineSegment(sketch, "E3.9.4.1", {"start": v(11.43, 5.08) * mm, "end": v(11.43, 6.34) * mm});
            skLineSegment(sketch, "E3.9.4.2", {"start": v(11.43, 5.08) * mm, "end": v(12.7, 5.08) * mm});
            skLineSegment(sketch, "E3.9.4.3", {"start": v(11.43, 6.34) * mm, "end": v(12.7, 6.34) * mm});
            skLineSegment(sketch, "E3.9.5.0", {"start": v(12.7, 6.35) * mm, "end": v(12.7, 7.61) * mm});
            skLineSegment(sketch, "E3.9.5.1", {"start": v(11.43, 6.35) * mm, "end": v(11.43, 7.61) * mm});
            skLineSegment(sketch, "E3.9.5.2", {"start": v(11.43, 6.35) * mm, "end": v(12.7, 6.35) * mm});
            skLineSegment(sketch, "E3.9.5.3", {"start": v(11.43, 7.61) * mm, "end": v(12.7, 7.61) * mm});
            skLineSegment(sketch, "E3.9.6.0", {"start": v(12.7, 7.62) * mm, "end": v(12.7, 8.88) * mm});
            skLineSegment(sketch, "E3.9.6.1", {"start": v(11.43, 7.62) * mm, "end": v(11.43, 8.88) * mm});
            skLineSegment(sketch, "E3.9.6.2", {"start": v(11.43, 7.62) * mm, "end": v(12.7, 7.62) * mm});
            skLineSegment(sketch, "E3.9.6.3", {"start": v(11.43, 8.88) * mm, "end": v(12.7, 8.88) * mm});
            skLineSegment(sketch, "E3.9.7.0", {"start": v(12.7, 8.9) * mm, "end": v(12.7, 10.15) * mm});
            skLineSegment(sketch, "E3.9.7.1", {"start": v(11.43, 8.9) * mm, "end": v(11.43, 10.15) * mm});
            skLineSegment(sketch, "E3.9.7.2", {"start": v(11.43, 8.9) * mm, "end": v(12.7, 8.9) * mm});
            skLineSegment(sketch, "E3.9.7.3", {"start": v(11.43, 10.15) * mm, "end": v(12.7, 10.15) * mm});
            skLineSegment(sketch, "E3.9.8.0", {"start": v(12.7, 10.16) * mm, "end": v(12.7, 11.42) * mm});
            skLineSegment(sketch, "E3.9.8.1", {"start": v(11.43, 10.16) * mm, "end": v(11.43, 11.42) * mm});
            skLineSegment(sketch, "E3.9.8.2", {"start": v(11.43, 10.16) * mm, "end": v(12.7, 10.16) * mm});
            skLineSegment(sketch, "E3.9.8.3", {"start": v(11.43, 11.42) * mm, "end": v(12.7, 11.42) * mm});
            skLineSegment(sketch, "E3.9.9.0", {"start": v(12.7, 11.43) * mm, "end": v(12.7, 12.7) * mm});
            skLineSegment(sketch, "E3.9.9.1", {"start": v(11.43, 11.43) * mm, "end": v(11.43, 12.7) * mm});
            skLineSegment(sketch, "E3.9.9.2", {"start": v(11.43, 11.43) * mm, "end": v(12.7, 11.43) * mm});
            skLineSegment(sketch, "E3.9.9.3", {"start": v(11.43, 12.7) * mm, "end": v(12.7, 12.7) * mm});
            skLineSegment(sketch, "E3.direction1", {"start": v(0, 0) * mm, "end": v(1.27, 0) * mm, "construction": true});
            skLineSegment(sketch, "E3.direction2", {"start": v(0, 0) * mm, "end": v(0, 1.27) * mm, "construction": true});
            skSolve(sketch);
        }
        {
            var Q0;
            Q0=makeQuery(id+"F3.imprint","IMPRINT",FACE,{"disambiguationData":[TD([[makeQuery(id+"F3.imprint","IMPRINT",EDGE,{"derivedFrom":sQuery(id+"F3.wireOp",EDGE,"E3.1.9.0")}),1.0]])]});
            var Q1;
            Q1=makeQuery(id+"F3.imprint","IMPRINT",FACE,{"disambiguationData":[TD([[makeQuery(id+"F3.imprint","IMPRINT",EDGE,{"derivedFrom":sQuery(id+"F3.wireOp",EDGE,"E3.0.8.0")}),1.0]])]});
            var Q2;
            Q2=makeQuery(id+"F3.imprint","IMPRINT",FACE,{"disambiguationData":[TD([[makeQuery(id+"F3.imprint","IMPRINT",EDGE,{"derivedFrom":sQuery(id+"F3.wireOp",EDGE,"E3.1.7.0")}),1.0]])]});
            var Q3;
            Q3=makeQuery(id+"F3.imprint","IMPRINT",FACE,{"disambiguationData":[TD([[makeQuery(id+"F3.imprint","IMPRINT",EDGE,{"derivedFrom":sQuery(id+"F3.wireOp",EDGE,"E3.2.8.0")}),1.0]])]});
            var Q4;
            Q4=makeQuery(id+"F3.imprint","IMPRINT",FACE,{"disambiguationData":[TD([[makeQuery(id+"F3.imprint","IMPRINT",EDGE,{"derivedFrom":sQuery(id+"F3.wireOp",EDGE,"E3.3.7.0")}),1.0]])]});
            var Q5;
            Q5=makeQuery(id+"F3.imprint","IMPRINT",FACE,{"disambiguationData":[TD([[makeQuery(id+"F3.imprint","IMPRINT",EDGE,{"derivedFrom":sQuery(id+"F3.wireOp",EDGE,"E3.2.6.0")}),1.0]])]});
            var Q6;
            Q6=makeQuery(id+"F3.imprint","IMPRINT",FACE,{"disambiguationData":[TD([[makeQuery(id+"F3.imprint","IMPRINT",EDGE,{"derivedFrom":sQuery(id+"F3.wireOp",EDGE,"E3.0.6.0")}),1.0]])]});
            var Q7;
            Q7=makeQuery(id+"F3.imprint","IMPRINT",FACE,{"disambiguationData":[TD([[makeQuery(id+"F3.imprint","IMPRINT",EDGE,{"derivedFrom":sQuery(id+"F3.wireOp",EDGE,"E3.1.5.0")}),1.0]])]});
            var Q8;
            Q8=makeQuery(id+"F3.imprint","IMPRINT",FACE,{"disambiguationData":[TD([[makeQuery(id+"F3.imprint","IMPRINT",EDGE,{"derivedFrom":sQuery(id+"F3.wireOp",EDGE,"E3.0.4.0")}),1.0]])]});
            var Q9;
            Q9=makeQuery(id+"F3.imprint","IMPRINT",FACE,{"disambiguationData":[TD([[makeQuery(id+"F3.imprint","IMPRINT",EDGE,{"derivedFrom":sQuery(id+"F3.wireOp",EDGE,"E2.bottom")}),1.0]])]});
            var Q10;
            Q10=makeQuery(id+"F3.imprint","IMPRINT",FACE,{"disambiguationData":[TD([[makeQuery(id+"F3.imprint","IMPRINT",EDGE,{"derivedFrom":sQuery(id+"F3.wireOp",EDGE,"E3.2.0.0")}),1.0]])]});
            var Q11;
            Q11=makeQuery(id+"F3.imprint","IMPRINT",FACE,{"disambiguationData":[TD([[makeQuery(id+"F3.imprint","IMPRINT",EDGE,{"derivedFrom":sQuery(id+"F3.wireOp",EDGE,"E3.2.2.0")}),1.0]])]});
            var Q12;
            Q12=makeQuery(id+"F3.imprint","IMPRINT",FACE,{"disambiguationData":[TD([[makeQuery(id+"F3.imprint","IMPRINT",EDGE,{"derivedFrom":sQuery(id+"F3.wireOp",EDGE,"E3.3.3.0")}),1.0]])]});
            var Q13;
            Q13=makeQuery(id+"F3.imprint","IMPRINT",FACE,{"disambiguationData":[TD([[makeQuery(id+"F3.imprint","IMPRINT",EDGE,{"derivedFrom":sQuery(id+"F3.wireOp",EDGE,"E3.2.4.0")}),1.0]])]});
            var Q14;
            Q14=makeQuery(id+"F3.imprint","IMPRINT",FACE,{"disambiguationData":[TD([[makeQuery(id+"F3.imprint","IMPRINT",EDGE,{"derivedFrom":sQuery(id+"F3.wireOp",EDGE,"E3.3.5.0")}),1.0]])]});
            var Q15;
            Q15=makeQuery(id+"F3.imprint","IMPRINT",FACE,{"disambiguationData":[TD([[makeQuery(id+"F3.imprint","IMPRINT",EDGE,{"derivedFrom":sQuery(id+"F3.wireOp",EDGE,"E3.4.4.0")}),1.0]])]});
            var Q16;
            Q16=makeQuery(id+"F3.imprint","IMPRINT",FACE,{"disambiguationData":[TD([[makeQuery(id+"F3.imprint","IMPRINT",EDGE,{"derivedFrom":sQuery(id+"F3.wireOp",EDGE,"E3.4.2.0")}),1.0]])]});
            var Q17;
            Q17=makeQuery(id+"F3.imprint","IMPRINT",FACE,{"disambiguationData":[TD([[makeQuery(id+"F3.imprint","IMPRINT",EDGE,{"derivedFrom":sQuery(id+"F3.wireOp",EDGE,"E3.3.1.0")}),1.0]])]});
            var Q18;
            Q18=makeQuery(id+"F3.imprint","IMPRINT",FACE,{"disambiguationData":[TD([[makeQuery(id+"F3.imprint","IMPRINT",EDGE,{"derivedFrom":sQuery(id+"F3.wireOp",EDGE,"E3.4.0.0")}),1.0]])]});
            var Q19;
            Q19=makeQuery(id+"F3.imprint","IMPRINT",FACE,{"disambiguationData":[TD([[makeQuery(id+"F3.imprint","IMPRINT",EDGE,{"derivedFrom":sQuery(id+"F3.wireOp",EDGE,"E3.5.1.0")}),1.0]])]});
            var Q20;
            Q20=makeQuery(id+"F3.imprint","IMPRINT",FACE,{"disambiguationData":[TD([[makeQuery(id+"F3.imprint","IMPRINT",EDGE,{"derivedFrom":sQuery(id+"F3.wireOp",EDGE,"E3.5.3.0")}),1.0]])]});
            var Q21;
            Q21=makeQuery(id+"F3.imprint","IMPRINT",FACE,{"disambiguationData":[TD([[makeQuery(id+"F3.imprint","IMPRINT",EDGE,{"derivedFrom":sQuery(id+"F3.wireOp",EDGE,"E3.7.3.0")}),1.0]])]});
            var Q22;
            Q22=makeQuery(id+"F3.imprint","IMPRINT",FACE,{"disambiguationData":[TD([[makeQuery(id+"F3.imprint","IMPRINT",EDGE,{"derivedFrom":sQuery(id+"F3.wireOp",EDGE,"E3.6.2.0")}),1.0]])]});
            var Q23;
            Q23=makeQuery(id+"F3.imprint","IMPRINT",FACE,{"disambiguationData":[TD([[makeQuery(id+"F3.imprint","IMPRINT",EDGE,{"derivedFrom":sQuery(id+"F3.wireOp",EDGE,"E3.7.1.0")}),1.0]])]});
            var Q24;
            Q24=makeQuery(id+"F3.imprint","IMPRINT",FACE,{"disambiguationData":[TD([[makeQuery(id+"F3.imprint","IMPRINT",EDGE,{"derivedFrom":sQuery(id+"F3.wireOp",EDGE,"E3.6.0.0")}),1.0]])]});
            var Q25;
            Q25=makeQuery(id+"F3.imprint","IMPRINT",FACE,{"disambiguationData":[TD([[makeQuery(id+"F3.imprint","IMPRINT",EDGE,{"derivedFrom":sQuery(id+"F3.wireOp",EDGE,"E3.8.0.0")}),1.0]])]});
            var Q26;
            Q26=makeQuery(id+"F3.imprint","IMPRINT",FACE,{"disambiguationData":[TD([[makeQuery(id+"F3.imprint","IMPRINT",EDGE,{"derivedFrom":sQuery(id+"F3.wireOp",EDGE,"E3.9.1.0")}),1.0]])]});
            var Q27;
            Q27=makeQuery(id+"F3.imprint","IMPRINT",FACE,{"disambiguationData":[TD([[makeQuery(id+"F3.imprint","IMPRINT",EDGE,{"derivedFrom":sQuery(id+"F3.wireOp",EDGE,"E3.8.2.0")}),1.0]])]});
            var Q28;
            Q28=makeQuery(id+"F3.imprint","IMPRINT",FACE,{"disambiguationData":[TD([[makeQuery(id+"F3.imprint","IMPRINT",EDGE,{"derivedFrom":sQuery(id+"F3.wireOp",EDGE,"E3.9.3.0")}),1.0]])]});
            var Q29;
            Q29=makeQuery(id+"F3.imprint","IMPRINT",FACE,{"disambiguationData":[TD([[makeQuery(id+"F3.imprint","IMPRINT",EDGE,{"derivedFrom":sQuery(id+"F3.wireOp",EDGE,"E3.8.4.0")}),1.0]])]});
            var Q30;
            Q30=makeQuery(id+"F3.imprint","IMPRINT",FACE,{"disambiguationData":[TD([[makeQuery(id+"F3.imprint","IMPRINT",EDGE,{"derivedFrom":sQuery(id+"F3.wireOp",EDGE,"E3.9.5.0")}),1.0]])]});
            var Q31;
            Q31=makeQuery(id+"F3.imprint","IMPRINT",FACE,{"disambiguationData":[TD([[makeQuery(id+"F3.imprint","IMPRINT",EDGE,{"derivedFrom":sQuery(id+"F3.wireOp",EDGE,"E3.7.5.0")}),1.0]])]});
            var Q32;
            Q32=makeQuery(id+"F3.imprint","IMPRINT",FACE,{"disambiguationData":[TD([[makeQuery(id+"F3.imprint","IMPRINT",EDGE,{"derivedFrom":sQuery(id+"F3.wireOp",EDGE,"E3.8.6.0")}),1.0]])]});
            var Q33;
            Q33=makeQuery(id+"F3.imprint","IMPRINT",FACE,{"disambiguationData":[TD([[makeQuery(id+"F3.imprint","IMPRINT",EDGE,{"derivedFrom":sQuery(id+"F3.wireOp",EDGE,"E3.9.7.0")}),1.0]])]});
            var Q34;
            Q34=makeQuery(id+"F3.imprint","IMPRINT",FACE,{"disambiguationData":[TD([[makeQuery(id+"F3.imprint","IMPRINT",EDGE,{"derivedFrom":sQuery(id+"F3.wireOp",EDGE,"E3.7.7.0")}),1.0]])]});
            var Q35;
            Q35=makeQuery(id+"F3.imprint","IMPRINT",FACE,{"disambiguationData":[TD([[makeQuery(id+"F3.imprint","IMPRINT",EDGE,{"derivedFrom":sQuery(id+"F3.wireOp",EDGE,"E3.8.8.0")}),1.0]])]});
            var Q36;
            Q36=makeQuery(id+"F3.imprint","IMPRINT",FACE,{"disambiguationData":[TD([[makeQuery(id+"F3.imprint","IMPRINT",EDGE,{"derivedFrom":sQuery(id+"F3.wireOp",EDGE,"E3.9.9.0")}),1.0]])]});
            var Q37;
            Q37=makeQuery(id+"F3.imprint","IMPRINT",FACE,{"disambiguationData":[TD([[makeQuery(id+"F3.imprint","IMPRINT",EDGE,{"derivedFrom":sQuery(id+"F3.wireOp",EDGE,"E3.7.9.0")}),1.0]])]});
            var Q38;
            Q38=makeQuery(id+"F3.imprint","IMPRINT",FACE,{"disambiguationData":[TD([[makeQuery(id+"F3.imprint","IMPRINT",EDGE,{"derivedFrom":sQuery(id+"F3.wireOp",EDGE,"E3.6.8.0")}),1.0]])]});
            var Q39;
            Q39=makeQuery(id+"F3.imprint","IMPRINT",FACE,{"disambiguationData":[TD([[makeQuery(id+"F3.imprint","IMPRINT",EDGE,{"derivedFrom":sQuery(id+"F3.wireOp",EDGE,"E3.5.7.0")}),1.0]])]});
            var Q40;
            Q40=makeQuery(id+"F3.imprint","IMPRINT",FACE,{"disambiguationData":[TD([[makeQuery(id+"F3.imprint","IMPRINT",EDGE,{"derivedFrom":sQuery(id+"F3.wireOp",EDGE,"E3.6.6.0")}),1.0]])]});
            var Q41;
            Q41=makeQuery(id+"F3.imprint","IMPRINT",FACE,{"disambiguationData":[TD([[makeQuery(id+"F3.imprint","IMPRINT",EDGE,{"derivedFrom":sQuery(id+"F3.wireOp",EDGE,"E3.4.6.0")}),1.0]])]});
            var Q42;
            Q42=makeQuery(id+"F3.imprint","IMPRINT",FACE,{"disambiguationData":[TD([[makeQuery(id+"F3.imprint","IMPRINT",EDGE,{"derivedFrom":sQuery(id+"F3.wireOp",EDGE,"E3.5.5.0")}),1.0]])]});
            var Q43;
            Q43=makeQuery(id+"F3.imprint","IMPRINT",FACE,{"disambiguationData":[TD([[makeQuery(id+"F3.imprint","IMPRINT",EDGE,{"derivedFrom":sQuery(id+"F3.wireOp",EDGE,"E3.4.8.0")}),1.0]])]});
            var Q44;
            Q44=makeQuery(id+"F3.imprint","IMPRINT",FACE,{"disambiguationData":[TD([[makeQuery(id+"F3.imprint","IMPRINT",EDGE,{"derivedFrom":sQuery(id+"F3.wireOp",EDGE,"E3.5.9.0")}),1.0]])]});
            var Q45;
            Q45=makeQuery(id+"F3.imprint","IMPRINT",FACE,{"disambiguationData":[TD([[makeQuery(id+"F3.imprint","IMPRINT",EDGE,{"derivedFrom":sQuery(id+"F3.wireOp",EDGE,"E3.3.9.0")}),1.0]])]});
            var Q46;
            Q46=makeQuery(id+"F3.imprint","IMPRINT",FACE,{"disambiguationData":[TD([[makeQuery(id+"F3.imprint","IMPRINT",EDGE,{"derivedFrom":sQuery(id+"F3.wireOp",EDGE,"E3.1.3.0")}),1.0]])]});
            var Q47;
            Q47=makeQuery(id+"F3.imprint","IMPRINT",FACE,{"disambiguationData":[TD([[makeQuery(id+"F3.imprint","IMPRINT",EDGE,{"derivedFrom":sQuery(id+"F3.wireOp",EDGE,"E3.0.2.0")}),1.0]])]});
            var Q48;
            Q48=makeQuery(id+"F3.imprint","IMPRINT",FACE,{"disambiguationData":[TD([[makeQuery(id+"F3.imprint","IMPRINT",EDGE,{"derivedFrom":sQuery(id+"F3.wireOp",EDGE,"E3.1.1.0")}),1.0]])]});
            var Q49;
            Q49=makeQuery(id+"F3.imprint","IMPRINT",FACE,{"disambiguationData":[TD([[makeQuery(id+"F3.imprint","IMPRINT",EDGE,{"derivedFrom":sQuery(id+"F3.wireOp",EDGE,"E3.6.4.0")}),1.0]])]});
            extrude(context, id + "F4", {"entities" : qUnion([Q0, Q1, Q2, Q3, Q4, Q5, Q6, Q7, Q8, Q9, Q10, Q11, Q12, Q13, Q14, Q15, Q16, Q17, Q18, Q19, Q20, Q21, Q22, Q23, Q24, Q25, Q26, Q27, Q28, Q29, Q30, Q31, Q32, Q33, Q34, Q35, Q36, Q37, Q38, Q39, Q40, Q41, Q42, Q43, Q44, Q45, Q46, Q47, Q48, Q49]), "depth" : 1.27 * mm});
        }
        {
            var Q0;
            Q0=makeQuery(id+"F4.opExtrude","CAP_FACE",FACE,{"disambiguationData":[OSD([sQuery(id+"F3.wireOp",EDGE,"E3.0.8.0"),sQuery(id+"F3.wireOp",EDGE,"E3.0.8.1"),sQuery(id+"F3.wireOp",EDGE,"E3.0.8.2"),sQuery(id+"F3.wireOp",EDGE,"E3.0.8.3")])],"isStart":false});
            var Q1;
            Q1=makeQuery(id+"F4.opExtrude","CAP_FACE",FACE,{"disambiguationData":[OSD([sQuery(id+"F3.wireOp",EDGE,"E3.2.8.0"),sQuery(id+"F3.wireOp",EDGE,"E3.2.8.1"),sQuery(id+"F3.wireOp",EDGE,"E3.2.8.2"),sQuery(id+"F3.wireOp",EDGE,"E3.2.8.3")])],"isStart":false});
            var Q2;
            Q2=makeQuery(id+"F4.opExtrude","CAP_FACE",FACE,{"disambiguationData":[OSD([sQuery(id+"F3.wireOp",EDGE,"E3.1.7.0"),sQuery(id+"F3.wireOp",EDGE,"E3.1.7.1"),sQuery(id+"F3.wireOp",EDGE,"E3.1.7.2"),sQuery(id+"F3.wireOp",EDGE,"E3.1.7.3")])],"isStart":false});
            var Q3;
            Q3=makeQuery(id+"F4.opExtrude","CAP_FACE",FACE,{"disambiguationData":[OSD([sQuery(id+"F3.wireOp",EDGE,"E3.0.6.0"),sQuery(id+"F3.wireOp",EDGE,"E3.0.6.1"),sQuery(id+"F3.wireOp",EDGE,"E3.0.6.2"),sQuery(id+"F3.wireOp",EDGE,"E3.0.6.3")])],"isStart":false});
            var Q4;
            Q4=makeQuery(id+"F4.opExtrude","CAP_FACE",FACE,{"disambiguationData":[OSD([sQuery(id+"F3.wireOp",EDGE,"E3.2.6.0"),sQuery(id+"F3.wireOp",EDGE,"E3.2.6.1"),sQuery(id+"F3.wireOp",EDGE,"E3.2.6.2"),sQuery(id+"F3.wireOp",EDGE,"E3.2.6.3")])],"isStart":false});
            var Q5;
            Q5=makeQuery(id+"F4.opExtrude","CAP_FACE",FACE,{"disambiguationData":[OSD([sQuery(id+"F3.wireOp",EDGE,"E3.1.5.0"),sQuery(id+"F3.wireOp",EDGE,"E3.1.5.1"),sQuery(id+"F3.wireOp",EDGE,"E3.1.5.2"),sQuery(id+"F3.wireOp",EDGE,"E3.1.5.3")])],"isStart":false});
            var Q6;
            Q6=makeQuery(id+"F4.opExtrude","CAP_FACE",FACE,{"disambiguationData":[OSD([sQuery(id+"F3.wireOp",EDGE,"E3.0.4.0"),sQuery(id+"F3.wireOp",EDGE,"E3.0.4.1"),sQuery(id+"F3.wireOp",EDGE,"E3.0.4.2"),sQuery(id+"F3.wireOp",EDGE,"E3.0.4.3")])],"isStart":false});
            var Q7;
            Q7=makeQuery(id+"F4.opExtrude","CAP_FACE",FACE,{"disambiguationData":[OSD([sQuery(id+"F3.wireOp",EDGE,"E3.2.4.0"),sQuery(id+"F3.wireOp",EDGE,"E3.2.4.1"),sQuery(id+"F3.wireOp",EDGE,"E3.2.4.2"),sQuery(id+"F3.wireOp",EDGE,"E3.2.4.3")])],"isStart":false});
            var Q8;
            Q8=makeQuery(id+"F4.opExtrude","CAP_FACE",FACE,{"disambiguationData":[OSD([sQuery(id+"F3.wireOp",EDGE,"E3.1.3.0"),sQuery(id+"F3.wireOp",EDGE,"E3.1.3.1"),sQuery(id+"F3.wireOp",EDGE,"E3.1.3.2"),sQuery(id+"F3.wireOp",EDGE,"E3.1.3.3")])],"isStart":false});
            var Q9;
            Q9=makeQuery(id+"F4.opExtrude","CAP_FACE",FACE,{"disambiguationData":[OSD([sQuery(id+"F3.wireOp",EDGE,"E3.0.2.0"),sQuery(id+"F3.wireOp",EDGE,"E3.0.2.1"),sQuery(id+"F3.wireOp",EDGE,"E3.0.2.2"),sQuery(id+"F3.wireOp",EDGE,"E3.0.2.3")])],"isStart":false});
            var Q10;
            Q10=makeQuery(id+"F4.opExtrude","CAP_FACE",FACE,{"disambiguationData":[OSD([sQuery(id+"F3.wireOp",EDGE,"E3.1.1.0"),sQuery(id+"F3.wireOp",EDGE,"E3.1.1.1"),sQuery(id+"F3.wireOp",EDGE,"E3.1.1.2"),sQuery(id+"F3.wireOp",EDGE,"E3.1.1.3")])],"isStart":false});
            var Q11;
            Q11=makeQuery(id+"F4.opExtrude","CAP_EDGE",EDGE,{"disambiguationData":[OSD([sQuery(id+"F3.wireOp",EDGE,"E3.2.2.0")])],"isStart":false});
            var Q12;
            Q12=makeQuery(id+"F4.opExtrude","CAP_FACE",FACE,{"disambiguationData":[OSD([sQuery(id+"F3.wireOp",EDGE,"E3.2.2.0"),sQuery(id+"F3.wireOp",EDGE,"E3.2.2.1"),sQuery(id+"F3.wireOp",EDGE,"E3.2.2.2"),sQuery(id+"F3.wireOp",EDGE,"E3.2.2.3")])],"isStart":false});
            var Q13;
            Q13=makeQuery(id+"F4.opExtrude","CAP_FACE",FACE,{"disambiguationData":[OSD([sQuery(id+"F3.wireOp",EDGE,"E2.bottom"),sQuery(id+"F3.wireOp",EDGE,"E2.top"),sQuery(id+"F3.wireOp",EDGE,"E2.left"),sQuery(id+"F3.wireOp",EDGE,"E2.right")])],"isStart":false});
            var Q14;
            Q14=makeQuery(id+"F4.opExtrude","CAP_FACE",FACE,{"disambiguationData":[OSD([sQuery(id+"F3.wireOp",EDGE,"E3.2.0.0"),sQuery(id+"F3.wireOp",EDGE,"E3.2.0.1"),sQuery(id+"F3.wireOp",EDGE,"E3.2.0.2"),sQuery(id+"F3.wireOp",EDGE,"E3.2.0.3")])],"isStart":false});
            var Q15;
            Q15=makeQuery(id+"F4.opExtrude","CAP_FACE",FACE,{"disambiguationData":[OSD([sQuery(id+"F3.wireOp",EDGE,"E3.4.0.0"),sQuery(id+"F3.wireOp",EDGE,"E3.4.0.1"),sQuery(id+"F3.wireOp",EDGE,"E3.4.0.2"),sQuery(id+"F3.wireOp",EDGE,"E3.4.0.3")])],"isStart":false});
            var Q16;
            Q16=makeQuery(id+"F4.opExtrude","CAP_FACE",FACE,{"disambiguationData":[OSD([sQuery(id+"F3.wireOp",EDGE,"E3.3.1.0"),sQuery(id+"F3.wireOp",EDGE,"E3.3.1.1"),sQuery(id+"F3.wireOp",EDGE,"E3.3.1.2"),sQuery(id+"F3.wireOp",EDGE,"E3.3.1.3")])],"isStart":false});
            var Q17;
            Q17=makeQuery(id+"F4.opExtrude","CAP_FACE",FACE,{"disambiguationData":[OSD([sQuery(id+"F3.wireOp",EDGE,"E3.4.2.0"),sQuery(id+"F3.wireOp",EDGE,"E3.4.2.1"),sQuery(id+"F3.wireOp",EDGE,"E3.4.2.2"),sQuery(id+"F3.wireOp",EDGE,"E3.4.2.3")])],"isStart":false});
            var Q18;
            Q18=makeQuery(id+"F4.opExtrude","CAP_FACE",FACE,{"disambiguationData":[OSD([sQuery(id+"F3.wireOp",EDGE,"E3.3.3.0"),sQuery(id+"F3.wireOp",EDGE,"E3.3.3.1"),sQuery(id+"F3.wireOp",EDGE,"E3.3.3.2"),sQuery(id+"F3.wireOp",EDGE,"E3.3.3.3")])],"isStart":false});
            var Q19;
            Q19=makeQuery(id+"F4.opExtrude","CAP_FACE",FACE,{"disambiguationData":[OSD([sQuery(id+"F3.wireOp",EDGE,"E3.4.4.0"),sQuery(id+"F3.wireOp",EDGE,"E3.4.4.1"),sQuery(id+"F3.wireOp",EDGE,"E3.4.4.2"),sQuery(id+"F3.wireOp",EDGE,"E3.4.4.3")])],"isStart":false});
            var Q20;
            Q20=makeQuery(id+"F4.opExtrude","CAP_FACE",FACE,{"disambiguationData":[OSD([sQuery(id+"F3.wireOp",EDGE,"E3.3.5.0"),sQuery(id+"F3.wireOp",EDGE,"E3.3.5.1"),sQuery(id+"F3.wireOp",EDGE,"E3.3.5.2"),sQuery(id+"F3.wireOp",EDGE,"E3.3.5.3")])],"isStart":false});
            var Q21;
            Q21=makeQuery(id+"F4.opExtrude","CAP_FACE",FACE,{"disambiguationData":[OSD([sQuery(id+"F3.wireOp",EDGE,"E3.4.6.0"),sQuery(id+"F3.wireOp",EDGE,"E3.4.6.1"),sQuery(id+"F3.wireOp",EDGE,"E3.4.6.2"),sQuery(id+"F3.wireOp",EDGE,"E3.4.6.3")])],"isStart":false});
            var Q22;
            Q22=makeQuery(id+"F4.opExtrude","CAP_FACE",FACE,{"disambiguationData":[OSD([sQuery(id+"F3.wireOp",EDGE,"E3.3.7.0"),sQuery(id+"F3.wireOp",EDGE,"E3.3.7.1"),sQuery(id+"F3.wireOp",EDGE,"E3.3.7.2"),sQuery(id+"F3.wireOp",EDGE,"E3.3.7.3")])],"isStart":false});
            var Q23;
            Q23=makeQuery(id+"F4.opExtrude","CAP_FACE",FACE,{"disambiguationData":[OSD([sQuery(id+"F3.wireOp",EDGE,"E3.4.8.0"),sQuery(id+"F3.wireOp",EDGE,"E3.4.8.1"),sQuery(id+"F3.wireOp",EDGE,"E3.4.8.2"),sQuery(id+"F3.wireOp",EDGE,"E3.4.8.3")])],"isStart":false});
            var Q24;
            Q24=makeQuery(id+"F4.opExtrude","CAP_FACE",FACE,{"disambiguationData":[OSD([sQuery(id+"F3.wireOp",EDGE,"E3.3.9.0"),sQuery(id+"F3.wireOp",EDGE,"E3.3.9.1"),sQuery(id+"F3.wireOp",EDGE,"E3.3.9.2"),sQuery(id+"F3.wireOp",EDGE,"E3.3.9.3")])],"isStart":false});
            var Q25;
            Q25=makeQuery(id+"F4.opExtrude","CAP_FACE",FACE,{"disambiguationData":[OSD([sQuery(id+"F3.wireOp",EDGE,"E3.5.9.0"),sQuery(id+"F3.wireOp",EDGE,"E3.5.9.1"),sQuery(id+"F3.wireOp",EDGE,"E3.5.9.2"),sQuery(id+"F3.wireOp",EDGE,"E3.5.9.3")])],"isStart":false});
            var Q26;
            Q26=makeQuery(id+"F4.opExtrude","CAP_FACE",FACE,{"disambiguationData":[OSD([sQuery(id+"F3.wireOp",EDGE,"E3.1.9.0"),sQuery(id+"F3.wireOp",EDGE,"E3.1.9.1"),sQuery(id+"F3.wireOp",EDGE,"E3.1.9.2"),sQuery(id+"F3.wireOp",EDGE,"E3.1.9.3")])],"isStart":false});
            var Q27;
            Q27=makeQuery(id+"F4.opExtrude","CAP_FACE",FACE,{"disambiguationData":[OSD([sQuery(id+"F3.wireOp",EDGE,"E3.6.8.0"),sQuery(id+"F3.wireOp",EDGE,"E3.6.8.1"),sQuery(id+"F3.wireOp",EDGE,"E3.6.8.2"),sQuery(id+"F3.wireOp",EDGE,"E3.6.8.3")])],"isStart":false});
            var Q28;
            Q28=makeQuery(id+"F4.opExtrude","CAP_FACE",FACE,{"disambiguationData":[OSD([sQuery(id+"F3.wireOp",EDGE,"E3.5.7.0"),sQuery(id+"F3.wireOp",EDGE,"E3.5.7.1"),sQuery(id+"F3.wireOp",EDGE,"E3.5.7.2"),sQuery(id+"F3.wireOp",EDGE,"E3.5.7.3")])],"isStart":false});
            var Q29;
            Q29=makeQuery(id+"F4.opExtrude","CAP_FACE",FACE,{"disambiguationData":[OSD([sQuery(id+"F3.wireOp",EDGE,"E3.6.6.0"),sQuery(id+"F3.wireOp",EDGE,"E3.6.6.1"),sQuery(id+"F3.wireOp",EDGE,"E3.6.6.2"),sQuery(id+"F3.wireOp",EDGE,"E3.6.6.3")])],"isStart":false});
            var Q30;
            Q30=makeQuery(id+"F4.opExtrude","CAP_FACE",FACE,{"disambiguationData":[OSD([sQuery(id+"F3.wireOp",EDGE,"E3.5.5.0"),sQuery(id+"F3.wireOp",EDGE,"E3.5.5.1"),sQuery(id+"F3.wireOp",EDGE,"E3.5.5.2"),sQuery(id+"F3.wireOp",EDGE,"E3.5.5.3")])],"isStart":false});
            var Q31;
            Q31=makeQuery(id+"F4.opExtrude","CAP_FACE",FACE,{"disambiguationData":[OSD([sQuery(id+"F3.wireOp",EDGE,"E3.6.4.0"),sQuery(id+"F3.wireOp",EDGE,"E3.6.4.1"),sQuery(id+"F3.wireOp",EDGE,"E3.6.4.2"),sQuery(id+"F3.wireOp",EDGE,"E3.6.4.3")])],"isStart":false});
            var Q32;
            Q32=makeQuery(id+"F4.opExtrude","CAP_FACE",FACE,{"disambiguationData":[OSD([sQuery(id+"F3.wireOp",EDGE,"E3.5.3.0"),sQuery(id+"F3.wireOp",EDGE,"E3.5.3.1"),sQuery(id+"F3.wireOp",EDGE,"E3.5.3.2"),sQuery(id+"F3.wireOp",EDGE,"E3.5.3.3")])],"isStart":false});
            var Q33;
            Q33=makeQuery(id+"F4.opExtrude","CAP_FACE",FACE,{"disambiguationData":[OSD([sQuery(id+"F3.wireOp",EDGE,"E3.6.2.0"),sQuery(id+"F3.wireOp",EDGE,"E3.6.2.1"),sQuery(id+"F3.wireOp",EDGE,"E3.6.2.2"),sQuery(id+"F3.wireOp",EDGE,"E3.6.2.3")])],"isStart":false});
            var Q34;
            Q34=makeQuery(id+"F4.opExtrude","CAP_FACE",FACE,{"disambiguationData":[OSD([sQuery(id+"F3.wireOp",EDGE,"E3.5.1.0"),sQuery(id+"F3.wireOp",EDGE,"E3.5.1.1"),sQuery(id+"F3.wireOp",EDGE,"E3.5.1.2"),sQuery(id+"F3.wireOp",EDGE,"E3.5.1.3")])],"isStart":false});
            var Q35;
            Q35=makeQuery(id+"F4.opExtrude","CAP_FACE",FACE,{"disambiguationData":[OSD([sQuery(id+"F3.wireOp",EDGE,"E3.6.0.0"),sQuery(id+"F3.wireOp",EDGE,"E3.6.0.1"),sQuery(id+"F3.wireOp",EDGE,"E3.6.0.2"),sQuery(id+"F3.wireOp",EDGE,"E3.6.0.3")])],"isStart":false});
            var Q36;
            Q36=makeQuery(id+"F4.opExtrude","CAP_FACE",FACE,{"disambiguationData":[OSD([sQuery(id+"F3.wireOp",EDGE,"E3.7.1.0"),sQuery(id+"F3.wireOp",EDGE,"E3.7.1.1"),sQuery(id+"F3.wireOp",EDGE,"E3.7.1.2"),sQuery(id+"F3.wireOp",EDGE,"E3.7.1.3")])],"isStart":false});
            var Q37;
            Q37=makeQuery(id+"F4.opExtrude","CAP_FACE",FACE,{"disambiguationData":[OSD([sQuery(id+"F3.wireOp",EDGE,"E3.8.0.0"),sQuery(id+"F3.wireOp",EDGE,"E3.8.0.1"),sQuery(id+"F3.wireOp",EDGE,"E3.8.0.2"),sQuery(id+"F3.wireOp",EDGE,"E3.8.0.3")])],"isStart":false});
            var Q38;
            Q38=makeQuery(id+"F4.opExtrude","CAP_FACE",FACE,{"disambiguationData":[OSD([sQuery(id+"F3.wireOp",EDGE,"E3.9.1.0"),sQuery(id+"F3.wireOp",EDGE,"E3.9.1.1"),sQuery(id+"F3.wireOp",EDGE,"E3.9.1.2"),sQuery(id+"F3.wireOp",EDGE,"E3.9.1.3")])],"isStart":false});
            var Q39;
            Q39=makeQuery(id+"F4.opExtrude","CAP_FACE",FACE,{"disambiguationData":[OSD([sQuery(id+"F3.wireOp",EDGE,"E3.8.2.0"),sQuery(id+"F3.wireOp",EDGE,"E3.8.2.1"),sQuery(id+"F3.wireOp",EDGE,"E3.8.2.2"),sQuery(id+"F3.wireOp",EDGE,"E3.8.2.3")])],"isStart":false});
            var Q40;
            Q40=makeQuery(id+"F4.opExtrude","CAP_FACE",FACE,{"disambiguationData":[OSD([sQuery(id+"F3.wireOp",EDGE,"E3.9.3.0"),sQuery(id+"F3.wireOp",EDGE,"E3.9.3.1"),sQuery(id+"F3.wireOp",EDGE,"E3.9.3.2"),sQuery(id+"F3.wireOp",EDGE,"E3.9.3.3")])],"isStart":false});
            var Q41;
            Q41=makeQuery(id+"F4.opExtrude","CAP_FACE",FACE,{"disambiguationData":[OSD([sQuery(id+"F3.wireOp",EDGE,"E3.7.3.0"),sQuery(id+"F3.wireOp",EDGE,"E3.7.3.1"),sQuery(id+"F3.wireOp",EDGE,"E3.7.3.2"),sQuery(id+"F3.wireOp",EDGE,"E3.7.3.3")])],"isStart":false});
            var Q42;
            Q42=makeQuery(id+"F4.opExtrude","CAP_FACE",FACE,{"disambiguationData":[OSD([sQuery(id+"F3.wireOp",EDGE,"E3.7.5.0"),sQuery(id+"F3.wireOp",EDGE,"E3.7.5.1"),sQuery(id+"F3.wireOp",EDGE,"E3.7.5.2"),sQuery(id+"F3.wireOp",EDGE,"E3.7.5.3")])],"isStart":false});
            var Q43;
            Q43=makeQuery(id+"F4.opExtrude","CAP_FACE",FACE,{"disambiguationData":[OSD([sQuery(id+"F3.wireOp",EDGE,"E3.9.5.0"),sQuery(id+"F3.wireOp",EDGE,"E3.9.5.1"),sQuery(id+"F3.wireOp",EDGE,"E3.9.5.2"),sQuery(id+"F3.wireOp",EDGE,"E3.9.5.3")])],"isStart":false});
            var Q44;
            Q44=makeQuery(id+"F4.opExtrude","CAP_FACE",FACE,{"disambiguationData":[OSD([sQuery(id+"F3.wireOp",EDGE,"E3.8.6.0"),sQuery(id+"F3.wireOp",EDGE,"E3.8.6.1"),sQuery(id+"F3.wireOp",EDGE,"E3.8.6.2"),sQuery(id+"F3.wireOp",EDGE,"E3.8.6.3")])],"isStart":false});
            var Q45;
            Q45=makeQuery(id+"F4.opExtrude","CAP_FACE",FACE,{"disambiguationData":[OSD([sQuery(id+"F3.wireOp",EDGE,"E3.7.7.0"),sQuery(id+"F3.wireOp",EDGE,"E3.7.7.1"),sQuery(id+"F3.wireOp",EDGE,"E3.7.7.2"),sQuery(id+"F3.wireOp",EDGE,"E3.7.7.3")])],"isStart":false});
            var Q46;
            Q46=makeQuery(id+"F4.opExtrude","CAP_FACE",FACE,{"disambiguationData":[OSD([sQuery(id+"F3.wireOp",EDGE,"E3.9.7.0"),sQuery(id+"F3.wireOp",EDGE,"E3.9.7.1"),sQuery(id+"F3.wireOp",EDGE,"E3.9.7.2"),sQuery(id+"F3.wireOp",EDGE,"E3.9.7.3")])],"isStart":false});
            var Q47;
            Q47=makeQuery(id+"F4.opExtrude","CAP_FACE",FACE,{"disambiguationData":[OSD([sQuery(id+"F3.wireOp",EDGE,"E3.8.8.0"),sQuery(id+"F3.wireOp",EDGE,"E3.8.8.1"),sQuery(id+"F3.wireOp",EDGE,"E3.8.8.2"),sQuery(id+"F3.wireOp",EDGE,"E3.8.8.3")])],"isStart":false});
            var Q48;
            Q48=makeQuery(id+"F4.opExtrude","CAP_FACE",FACE,{"disambiguationData":[OSD([sQuery(id+"F3.wireOp",EDGE,"E3.7.9.0"),sQuery(id+"F3.wireOp",EDGE,"E3.7.9.1"),sQuery(id+"F3.wireOp",EDGE,"E3.7.9.2"),sQuery(id+"F3.wireOp",EDGE,"E3.7.9.3")])],"isStart":false});
            var Q49;
            Q49=makeQuery(id+"F4.opExtrude","CAP_FACE",FACE,{"disambiguationData":[OSD([sQuery(id+"F3.wireOp",EDGE,"E3.9.9.0"),sQuery(id+"F3.wireOp",EDGE,"E3.9.9.1"),sQuery(id+"F3.wireOp",EDGE,"E3.9.9.2"),sQuery(id+"F3.wireOp",EDGE,"E3.9.9.3")])],"isStart":false});
            var Q50;
            Q50=makeQuery(id+"F4.opExtrude","CAP_FACE",FACE,{"disambiguationData":[OSD([sQuery(id+"F3.wireOp",EDGE,"E3.8.4.0"),sQuery(id+"F3.wireOp",EDGE,"E3.8.4.1"),sQuery(id+"F3.wireOp",EDGE,"E3.8.4.2"),sQuery(id+"F3.wireOp",EDGE,"E3.8.4.3")])],"isStart":false});
            chamfer(context, id + "F5", {"entities" : qUnion([Q0, Q1, Q2, Q3, Q4, Q5, Q6, Q7, Q8, Q9, Q10, Q11, Q12, Q13, Q14, Q15, Q16, Q17, Q18, Q19, Q20, Q21, Q22, Q23, Q24, Q25, Q26, Q27, Q28, Q29, Q30, Q31, Q32, Q33, Q34, Q35, Q36, Q37, Q38, Q39, Q40, Q41, Q42, Q43, Q44, Q45, Q46, Q47, Q48, Q49, Q50]), "width" : 0.58 * mm, "tangentPropagation" : true});
        }
    });
